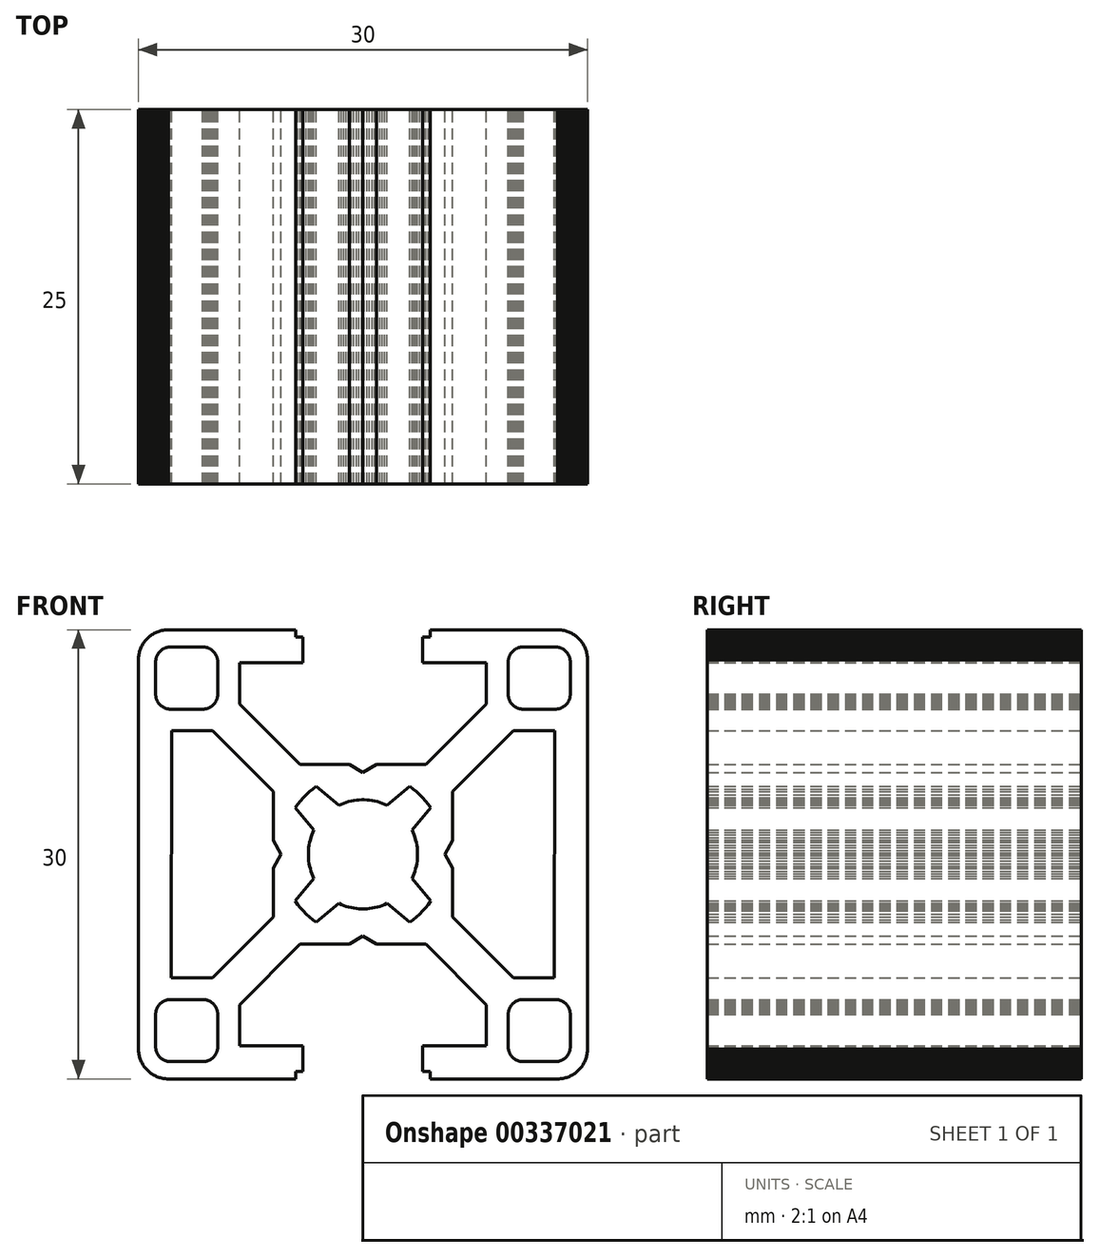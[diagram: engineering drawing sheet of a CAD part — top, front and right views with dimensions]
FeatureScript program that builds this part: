
annotation { "Feature Type Name" : "Feature", "Feature Type Description" : "" }
export const myFeature = defineFeature(function(context is Context, id is Id, definition is map)
    precondition{}
    {
        {
            var Q0;
            Q0=qCreatedBy(makeId("Front.planeOp"),FACE);
            var sketch = newSketch(context, id + "F0", { "sketchPlane" : qUnion([Q0])});
            skLineSegment(sketch, "E0", {"start": v(9.7, -12.9) * mm, "end": v(9.7, -12.85) * mm});
            skLineSegment(sketch, "E1", {"start": v(-13.85, -12.9) * mm, "end": v(-13.85, -12.85) * mm});
            skLineSegment(sketch, "E2", {"start": v(13.85, -10.7) * mm, "end": v(13.85, -10.66) * mm});
            skLineSegment(sketch, "E3", {"start": v(-9.7, -10.7) * mm, "end": v(-9.7, -10.66) * mm});
            skLineSegment(sketch, "E4", {"start": v(9.7, 10.66) * mm, "end": v(9.7, 10.7) * mm});
            skLineSegment(sketch, "E5", {"start": v(-13.85, 10.66) * mm, "end": v(-13.85, 10.7) * mm});
            skLineSegment(sketch, "E6", {"start": v(13.85, 12.85) * mm, "end": v(13.85, 12.9) * mm});
            skLineSegment(sketch, "E7", {"start": v(-9.7, 12.85) * mm, "end": v(-9.7, 12.9) * mm});
            skLineSegment(sketch, "E8", {"start": v(-15, -13.09) * mm, "end": v(-15, -13) * mm});
            skLineSegment(sketch, "E9", {"start": v(15, 13) * mm, "end": v(15, 13.09) * mm});
            skLineSegment(sketch, "E10", {"start": v(-3.64, -0.26) * mm, "end": v(-3.65, -0.09) * mm});
            skLineSegment(sketch, "E11", {"start": v(3.65, 0.09) * mm, "end": v(3.64, 0.26) * mm});
            skLineSegment(sketch, "E12", {"start": v(9.7, -12.94) * mm, "end": v(9.7, -12.9) * mm});
            skLineSegment(sketch, "E13", {"start": v(-9.7, -10.66) * mm, "end": v(-9.7, -10.61) * mm});
            skLineSegment(sketch, "E14", {"start": v(9.7, 10.61) * mm, "end": v(9.7, 10.66) * mm});
            skLineSegment(sketch, "E15", {"start": v(-9.7, 12.9) * mm, "end": v(-9.7, 12.94) * mm});
            skLineSegment(sketch, "E16", {"start": v(-15, -13.18) * mm, "end": v(-15, -13.09) * mm});
            skLineSegment(sketch, "E17", {"start": v(15, 13.09) * mm, "end": v(15, 13.18) * mm});
            skLineSegment(sketch, "E18", {"start": v(-13.85, -12.94) * mm, "end": v(-13.85, -12.9) * mm});
            skLineSegment(sketch, "E19", {"start": v(13.85, -10.66) * mm, "end": v(13.85, -10.61) * mm});
            skLineSegment(sketch, "E20", {"start": v(-13.85, 10.61) * mm, "end": v(-13.85, 10.66) * mm});
            skLineSegment(sketch, "E21", {"start": v(13.85, 12.9) * mm, "end": v(13.85, 12.94) * mm});
            skLineSegment(sketch, "E22", {"start": v(-3.62, -0.44) * mm, "end": v(-3.64, -0.26) * mm});
            skLineSegment(sketch, "E23", {"start": v(3.64, 0.26) * mm, "end": v(3.62, 0.44) * mm});
            skLineSegment(sketch, "E24", {"start": v(13.85, -10.61) * mm, "end": v(13.84, -10.57) * mm});
            skLineSegment(sketch, "E25", {"start": v(-13.84, 10.57) * mm, "end": v(-13.85, 10.61) * mm});
            skLineSegment(sketch, "E26", {"start": v(-13.84, -12.98) * mm, "end": v(-13.85, -12.94) * mm});
            skLineSegment(sketch, "E27", {"start": v(13.85, 12.94) * mm, "end": v(13.84, 12.98) * mm});
            skLineSegment(sketch, "E28", {"start": v(-14.98, -13.27) * mm, "end": v(-15, -13.18) * mm});
            skLineSegment(sketch, "E29", {"start": v(15, 13.18) * mm, "end": v(14.98, 13.27) * mm});
            skLineSegment(sketch, "E30", {"start": v(-9.7, -10.61) * mm, "end": v(-9.7, -10.57) * mm});
            skLineSegment(sketch, "E31", {"start": v(9.7, 10.57) * mm, "end": v(9.7, 10.61) * mm});
            skLineSegment(sketch, "E32", {"start": v(9.7, -12.98) * mm, "end": v(9.7, -12.94) * mm});
            skLineSegment(sketch, "E33", {"start": v(-9.7, 12.94) * mm, "end": v(-9.7, 12.98) * mm});
            skLineSegment(sketch, "E34", {"start": v(-3.6, -0.61) * mm, "end": v(-3.62, -0.44) * mm});
            skLineSegment(sketch, "E35", {"start": v(3.62, 0.44) * mm, "end": v(3.6, 0.61) * mm});
            skLineSegment(sketch, "E36", {"start": v(9.72, -13.03) * mm, "end": v(9.7, -12.98) * mm});
            skLineSegment(sketch, "E37", {"start": v(-13.83, -13.03) * mm, "end": v(-13.84, -12.98) * mm});
            skLineSegment(sketch, "E38", {"start": v(13.84, 12.98) * mm, "end": v(13.83, 13.03) * mm});
            skLineSegment(sketch, "E39", {"start": v(-9.7, 12.98) * mm, "end": v(-9.72, 13.03) * mm});
            skLineSegment(sketch, "E40", {"start": v(-14.97, -13.36) * mm, "end": v(-14.98, -13.27) * mm});
            skLineSegment(sketch, "E41", {"start": v(14.98, 13.27) * mm, "end": v(14.97, 13.36) * mm});
            skLineSegment(sketch, "E42", {"start": v(13.84, -10.57) * mm, "end": v(13.83, -10.52) * mm});
            skLineSegment(sketch, "E43", {"start": v(-9.7, -10.57) * mm, "end": v(-9.72, -10.52) * mm});
            skLineSegment(sketch, "E44", {"start": v(9.72, 10.52) * mm, "end": v(9.7, 10.57) * mm});
            skLineSegment(sketch, "E45", {"start": v(-13.83, 10.52) * mm, "end": v(-13.84, 10.57) * mm});
            skLineSegment(sketch, "E46", {"start": v(-3.56, -0.79) * mm, "end": v(-3.6, -0.61) * mm});
            skLineSegment(sketch, "E47", {"start": v(3.6, 0.61) * mm, "end": v(3.56, 0.79) * mm});
            skLineSegment(sketch, "E48", {"start": v(-14.95, -13.45) * mm, "end": v(-14.97, -13.36) * mm});
            skLineSegment(sketch, "E49", {"start": v(14.97, 13.36) * mm, "end": v(14.95, 13.45) * mm});
            skLineSegment(sketch, "E50", {"start": v(9.73, -13.07) * mm, "end": v(9.72, -13.03) * mm});
            skLineSegment(sketch, "E51", {"start": v(-13.82, -13.07) * mm, "end": v(-13.83, -13.03) * mm});
            skLineSegment(sketch, "E52", {"start": v(13.83, -10.52) * mm, "end": v(13.82, -10.48) * mm});
            skLineSegment(sketch, "E53", {"start": v(-9.72, -10.52) * mm, "end": v(-9.73, -10.48) * mm});
            skLineSegment(sketch, "E54", {"start": v(9.73, 10.48) * mm, "end": v(9.72, 10.52) * mm});
            skLineSegment(sketch, "E55", {"start": v(-13.82, 10.48) * mm, "end": v(-13.83, 10.52) * mm});
            skLineSegment(sketch, "E56", {"start": v(13.83, 13.03) * mm, "end": v(13.82, 13.07) * mm});
            skLineSegment(sketch, "E57", {"start": v(-9.72, 13.03) * mm, "end": v(-9.73, 13.07) * mm});
            skLineSegment(sketch, "E58", {"start": v(-3.52, -0.96) * mm, "end": v(-3.56, -0.79) * mm});
            skLineSegment(sketch, "E59", {"start": v(3.56, 0.79) * mm, "end": v(3.52, 0.96) * mm});
            skLineSegment(sketch, "E60", {"start": v(-14.93, -13.53) * mm, "end": v(-14.95, -13.45) * mm});
            skLineSegment(sketch, "E61", {"start": v(13.82, -10.48) * mm, "end": v(13.81, -10.43) * mm});
            skLineSegment(sketch, "E62", {"start": v(-9.73, -10.48) * mm, "end": v(-9.74, -10.43) * mm});
            skLineSegment(sketch, "E63", {"start": v(9.74, 10.43) * mm, "end": v(9.73, 10.48) * mm});
            skLineSegment(sketch, "E64", {"start": v(-13.81, 10.43) * mm, "end": v(-13.82, 10.48) * mm});
            skLineSegment(sketch, "E65", {"start": v(14.95, 13.45) * mm, "end": v(14.93, 13.53) * mm});
            skLineSegment(sketch, "E66", {"start": v(9.74, -13.12) * mm, "end": v(9.73, -13.07) * mm});
            skLineSegment(sketch, "E67", {"start": v(-13.81, -13.12) * mm, "end": v(-13.82, -13.07) * mm});
            skLineSegment(sketch, "E68", {"start": v(13.82, 13.07) * mm, "end": v(13.81, 13.12) * mm});
            skLineSegment(sketch, "E69", {"start": v(-9.73, 13.07) * mm, "end": v(-9.74, 13.12) * mm});
            skLineSegment(sketch, "E70", {"start": v(-3.47, -1.13) * mm, "end": v(-3.52, -0.96) * mm});
            skLineSegment(sketch, "E71", {"start": v(3.52, 0.96) * mm, "end": v(3.47, 1.13) * mm});
            skLineSegment(sketch, "E72", {"start": v(9.75, -13.16) * mm, "end": v(9.74, -13.12) * mm});
            skLineSegment(sketch, "E73", {"start": v(-13.8, -13.16) * mm, "end": v(-13.81, -13.12) * mm});
            skLineSegment(sketch, "E74", {"start": v(13.81, 13.12) * mm, "end": v(13.8, 13.16) * mm});
            skLineSegment(sketch, "E75", {"start": v(-9.74, 13.12) * mm, "end": v(-9.75, 13.16) * mm});
            skLineSegment(sketch, "E76", {"start": v(13.81, -10.43) * mm, "end": v(13.8, -10.4) * mm});
            skLineSegment(sketch, "E77", {"start": v(-9.74, -10.43) * mm, "end": v(-9.75, -10.4) * mm});
            skLineSegment(sketch, "E78", {"start": v(9.75, 10.4) * mm, "end": v(9.74, 10.43) * mm});
            skLineSegment(sketch, "E79", {"start": v(-13.8, 10.4) * mm, "end": v(-13.81, 10.43) * mm});
            skLineSegment(sketch, "E80", {"start": v(-14.9, -13.62) * mm, "end": v(-14.93, -13.53) * mm});
            skLineSegment(sketch, "E81", {"start": v(14.93, 13.53) * mm, "end": v(14.9, 13.62) * mm});
            skLineSegment(sketch, "E82", {"start": v(-14.87, -13.7) * mm, "end": v(-14.9, -13.62) * mm});
            skLineSegment(sketch, "E83", {"start": v(14.9, 13.62) * mm, "end": v(14.87, 13.7) * mm});
            skLineSegment(sketch, "E84", {"start": v(9.76, -13.2) * mm, "end": v(9.75, -13.16) * mm});
            skLineSegment(sketch, "E85", {"start": v(-13.79, -13.2) * mm, "end": v(-13.8, -13.16) * mm});
            skLineSegment(sketch, "E86", {"start": v(13.8, -10.4) * mm, "end": v(13.79, -10.35) * mm});
            skLineSegment(sketch, "E87", {"start": v(-9.75, -10.4) * mm, "end": v(-9.76, -10.35) * mm});
            skLineSegment(sketch, "E88", {"start": v(9.76, 10.35) * mm, "end": v(9.75, 10.4) * mm});
            skLineSegment(sketch, "E89", {"start": v(-13.79, 10.35) * mm, "end": v(-13.8, 10.4) * mm});
            skLineSegment(sketch, "E90", {"start": v(13.8, 13.16) * mm, "end": v(13.79, 13.2) * mm});
            skLineSegment(sketch, "E91", {"start": v(-9.75, 13.16) * mm, "end": v(-9.76, 13.2) * mm});
            skLineSegment(sketch, "E92", {"start": v(-3.41, -1.3) * mm, "end": v(-3.47, -1.13) * mm});
            skLineSegment(sketch, "E93", {"start": v(3.47, 1.13) * mm, "end": v(3.41, 1.3) * mm});
            skLineSegment(sketch, "E94", {"start": v(-14.84, -13.79) * mm, "end": v(-14.87, -13.7) * mm});
            skLineSegment(sketch, "E95", {"start": v(14.87, 13.7) * mm, "end": v(14.84, 13.79) * mm});
            skLineSegment(sketch, "E96", {"start": v(9.78, -13.24) * mm, "end": v(9.76, -13.2) * mm});
            skLineSegment(sketch, "E97", {"start": v(-9.76, -10.35) * mm, "end": v(-9.78, -10.3) * mm});
            skLineSegment(sketch, "E98", {"start": v(9.78, 10.3) * mm, "end": v(9.76, 10.35) * mm});
            skLineSegment(sketch, "E99", {"start": v(-9.76, 13.2) * mm, "end": v(-9.78, 13.24) * mm});
            skLineSegment(sketch, "E100", {"start": v(-13.77, -13.24) * mm, "end": v(-13.79, -13.2) * mm});
            skLineSegment(sketch, "E101", {"start": v(13.79, -10.35) * mm, "end": v(13.77, -10.3) * mm});
            skLineSegment(sketch, "E102", {"start": v(-13.77, 10.3) * mm, "end": v(-13.79, 10.35) * mm});
            skLineSegment(sketch, "E103", {"start": v(13.79, 13.2) * mm, "end": v(13.77, 13.24) * mm});
            skLineSegment(sketch, "E104", {"start": v(-3.35, -1.46) * mm, "end": v(-3.41, -1.3) * mm});
            skLineSegment(sketch, "E105", {"start": v(3.41, 1.3) * mm, "end": v(3.35, 1.46) * mm});
            skLineSegment(sketch, "E106", {"start": v(-13.75, -13.28) * mm, "end": v(-13.77, -13.24) * mm});
            skLineSegment(sketch, "E107", {"start": v(13.77, -10.3) * mm, "end": v(13.75, -10.27) * mm});
            skLineSegment(sketch, "E108", {"start": v(-13.75, 10.27) * mm, "end": v(-13.77, 10.3) * mm});
            skLineSegment(sketch, "E109", {"start": v(13.77, 13.24) * mm, "end": v(13.75, 13.28) * mm});
            skLineSegment(sketch, "E110", {"start": v(9.8, -13.28) * mm, "end": v(9.78, -13.24) * mm});
            skLineSegment(sketch, "E111", {"start": v(-9.78, -10.3) * mm, "end": v(-9.8, -10.27) * mm});
            skLineSegment(sketch, "E112", {"start": v(9.8, 10.27) * mm, "end": v(9.78, 10.3) * mm});
            skLineSegment(sketch, "E113", {"start": v(-9.78, 13.24) * mm, "end": v(-9.8, 13.28) * mm});
            skLineSegment(sketch, "E114", {"start": v(-14.8, -13.87) * mm, "end": v(-14.84, -13.79) * mm});
            skLineSegment(sketch, "E115", {"start": v(14.84, 13.79) * mm, "end": v(14.8, 13.87) * mm});
            skLineSegment(sketch, "E116", {"start": v(-3.27, -1.62) * mm, "end": v(-3.35, -1.46) * mm});
            skLineSegment(sketch, "E117", {"start": v(3.35, 1.46) * mm, "end": v(3.27, 1.62) * mm});
            skLineSegment(sketch, "E118", {"start": v(-13.73, -13.32) * mm, "end": v(-13.75, -13.28) * mm});
            skLineSegment(sketch, "E119", {"start": v(13.75, -10.27) * mm, "end": v(13.73, -10.23) * mm});
            skLineSegment(sketch, "E120", {"start": v(-13.73, 10.23) * mm, "end": v(-13.75, 10.27) * mm});
            skLineSegment(sketch, "E121", {"start": v(13.75, 13.28) * mm, "end": v(13.73, 13.32) * mm});
            skLineSegment(sketch, "E122", {"start": v(-14.76, -13.95) * mm, "end": v(-14.8, -13.87) * mm});
            skLineSegment(sketch, "E123", {"start": v(14.8, 13.87) * mm, "end": v(14.76, 13.95) * mm});
            skLineSegment(sketch, "E124", {"start": v(9.82, -13.32) * mm, "end": v(9.8, -13.28) * mm});
            skLineSegment(sketch, "E125", {"start": v(-9.8, -10.27) * mm, "end": v(-9.82, -10.23) * mm});
            skLineSegment(sketch, "E126", {"start": v(9.82, 10.23) * mm, "end": v(9.8, 10.27) * mm});
            skLineSegment(sketch, "E127", {"start": v(-9.8, 13.28) * mm, "end": v(-9.82, 13.32) * mm});
            skLineSegment(sketch, "E128", {"start": v(-9.82, -10.23) * mm, "end": v(-9.84, -10.19) * mm});
            skLineSegment(sketch, "E129", {"start": v(9.84, 10.19) * mm, "end": v(9.82, 10.23) * mm});
            skLineSegment(sketch, "E130", {"start": v(9.84, -13.36) * mm, "end": v(9.82, -13.32) * mm});
            skLineSegment(sketch, "E131", {"start": v(-9.82, 13.32) * mm, "end": v(-9.84, 13.36) * mm});
            skLineSegment(sketch, "E132", {"start": v(-14.72, -14.03) * mm, "end": v(-14.76, -13.95) * mm});
            skLineSegment(sketch, "E133", {"start": v(14.76, 13.95) * mm, "end": v(14.72, 14.03) * mm});
            skLineSegment(sketch, "E134", {"start": v(13.73, -10.23) * mm, "end": v(13.7, -10.19) * mm});
            skLineSegment(sketch, "E135", {"start": v(-13.7, 10.19) * mm, "end": v(-13.73, 10.23) * mm});
            skLineSegment(sketch, "E136", {"start": v(-13.7, -13.36) * mm, "end": v(-13.73, -13.32) * mm});
            skLineSegment(sketch, "E137", {"start": v(13.73, 13.32) * mm, "end": v(13.7, 13.36) * mm});
            skLineSegment(sketch, "E138", {"start": v(6, -0.92) * mm, "end": v(5.47, 0) * mm});
            skLineSegment(sketch, "E139", {"start": v(-5.47, 0) * mm, "end": v(-6, 0.92) * mm});
            skLineSegment(sketch, "E140", {"start": v(-13.68, -13.4) * mm, "end": v(-13.7, -13.36) * mm});
            skLineSegment(sketch, "E141", {"start": v(13.7, 13.36) * mm, "end": v(13.68, 13.4) * mm});
            skLineSegment(sketch, "E142", {"start": v(13.7, -10.19) * mm, "end": v(13.68, -10.15) * mm});
            skLineSegment(sketch, "E143", {"start": v(-13.68, 10.15) * mm, "end": v(-13.7, 10.19) * mm});
            skLineSegment(sketch, "E144", {"start": v(-14.67, -14.1) * mm, "end": v(-14.72, -14.03) * mm});
            skLineSegment(sketch, "E145", {"start": v(14.72, 14.03) * mm, "end": v(14.67, 14.1) * mm});
            skLineSegment(sketch, "E146", {"start": v(9.87, -13.4) * mm, "end": v(9.84, -13.36) * mm});
            skLineSegment(sketch, "E147", {"start": v(-9.84, 13.36) * mm, "end": v(-9.87, 13.4) * mm});
            skLineSegment(sketch, "E148", {"start": v(-9.84, -10.19) * mm, "end": v(-9.87, -10.15) * mm});
            skLineSegment(sketch, "E149", {"start": v(9.87, 10.15) * mm, "end": v(9.84, 10.19) * mm});
            skLineSegment(sketch, "E150", {"start": v(9.9, -13.44) * mm, "end": v(9.87, -13.4) * mm});
            skLineSegment(sketch, "E151", {"start": v(-13.66, -13.44) * mm, "end": v(-13.68, -13.4) * mm});
            skLineSegment(sketch, "E152", {"start": v(13.68, -10.15) * mm, "end": v(13.66, -10.11) * mm});
            skLineSegment(sketch, "E153", {"start": v(-9.87, -10.15) * mm, "end": v(-9.9, -10.11) * mm});
            skLineSegment(sketch, "E154", {"start": v(9.9, 10.11) * mm, "end": v(9.87, 10.15) * mm});
            skLineSegment(sketch, "E155", {"start": v(-13.66, 10.11) * mm, "end": v(-13.68, 10.15) * mm});
            skLineSegment(sketch, "E156", {"start": v(13.68, 13.4) * mm, "end": v(13.66, 13.44) * mm});
            skLineSegment(sketch, "E157", {"start": v(-9.87, 13.4) * mm, "end": v(-9.9, 13.44) * mm});
            skLineSegment(sketch, "E158", {"start": v(-14.62, -14.18) * mm, "end": v(-14.67, -14.1) * mm});
            skLineSegment(sketch, "E159", {"start": v(14.67, 14.1) * mm, "end": v(14.62, 14.18) * mm});
            skLineSegment(sketch, "E160", {"start": v(-4.36, -3.35) * mm, "end": v(-4.53, -3.12) * mm});
            skLineSegment(sketch, "E161", {"start": v(4.53, 3.12) * mm, "end": v(4.36, 3.35) * mm});
            skLineSegment(sketch, "E162", {"start": v(9.92, -13.47) * mm, "end": v(9.9, -13.44) * mm});
            skLineSegment(sketch, "E163", {"start": v(-9.9, -10.11) * mm, "end": v(-9.92, -10.08) * mm});
            skLineSegment(sketch, "E164", {"start": v(9.92, 10.08) * mm, "end": v(9.9, 10.11) * mm});
            skLineSegment(sketch, "E165", {"start": v(-9.9, 13.44) * mm, "end": v(-9.92, 13.47) * mm});
            skLineSegment(sketch, "E166", {"start": v(-14.56, -14.25) * mm, "end": v(-14.62, -14.18) * mm});
            skLineSegment(sketch, "E167", {"start": v(14.62, 14.18) * mm, "end": v(14.56, 14.25) * mm});
            skLineSegment(sketch, "E168", {"start": v(-13.63, -13.47) * mm, "end": v(-13.66, -13.44) * mm});
            skLineSegment(sketch, "E169", {"start": v(13.66, -10.11) * mm, "end": v(13.63, -10.08) * mm});
            skLineSegment(sketch, "E170", {"start": v(-13.63, 10.08) * mm, "end": v(-13.66, 10.11) * mm});
            skLineSegment(sketch, "E171", {"start": v(13.66, 13.44) * mm, "end": v(13.63, 13.47) * mm});
            skLineSegment(sketch, "E172", {"start": v(-4.18, -3.57) * mm, "end": v(-4.36, -3.35) * mm});
            skLineSegment(sketch, "E173", {"start": v(4.36, 3.35) * mm, "end": v(4.18, 3.57) * mm});
            skLineSegment(sketch, "E174", {"start": v(-14.5, -14.32) * mm, "end": v(-14.56, -14.25) * mm});
            skLineSegment(sketch, "E175", {"start": v(13.63, -10.08) * mm, "end": v(13.6, -10.04) * mm});
            skLineSegment(sketch, "E176", {"start": v(-13.6, 10.04) * mm, "end": v(-13.63, 10.08) * mm});
            skLineSegment(sketch, "E177", {"start": v(14.56, 14.25) * mm, "end": v(14.5, 14.32) * mm});
            skLineSegment(sketch, "E178", {"start": v(-13.6, -13.5) * mm, "end": v(-13.63, -13.47) * mm});
            skLineSegment(sketch, "E179", {"start": v(13.63, 13.47) * mm, "end": v(13.6, 13.5) * mm});
            skLineSegment(sketch, "E180", {"start": v(-9.92, -10.08) * mm, "end": v(-9.95, -10.04) * mm});
            skLineSegment(sketch, "E181", {"start": v(9.95, 10.04) * mm, "end": v(9.92, 10.08) * mm});
            skLineSegment(sketch, "E182", {"start": v(9.95, -13.5) * mm, "end": v(9.92, -13.47) * mm});
            skLineSegment(sketch, "E183", {"start": v(-9.92, 13.47) * mm, "end": v(-9.95, 13.5) * mm});
            skLineSegment(sketch, "E184", {"start": v(4.53, -3.12) * mm, "end": v(3.27, -1.62) * mm});
            skLineSegment(sketch, "E185", {"start": v(-3.27, 1.62) * mm, "end": v(-4.53, 3.12) * mm});
            skLineSegment(sketch, "E186", {"start": v(-3.99, -3.79) * mm, "end": v(-4.18, -3.57) * mm});
            skLineSegment(sketch, "E187", {"start": v(4.18, 3.57) * mm, "end": v(3.99, 3.79) * mm});
            skLineSegment(sketch, "E188", {"start": v(9.98, -13.54) * mm, "end": v(9.95, -13.5) * mm});
            skLineSegment(sketch, "E189", {"start": v(-13.57, -13.54) * mm, "end": v(-13.6, -13.5) * mm});
            skLineSegment(sketch, "E190", {"start": v(13.6, -10.04) * mm, "end": v(13.57, -10) * mm});
            skLineSegment(sketch, "E191", {"start": v(-9.95, -10.04) * mm, "end": v(-9.98, -10) * mm});
            skLineSegment(sketch, "E192", {"start": v(9.98, 10) * mm, "end": v(9.95, 10.04) * mm});
            skLineSegment(sketch, "E193", {"start": v(-13.57, 10) * mm, "end": v(-13.6, 10.04) * mm});
            skLineSegment(sketch, "E194", {"start": v(13.6, 13.5) * mm, "end": v(13.57, 13.54) * mm});
            skLineSegment(sketch, "E195", {"start": v(-9.95, 13.5) * mm, "end": v(-9.98, 13.54) * mm});
            skLineSegment(sketch, "E196", {"start": v(-14.45, -14.38) * mm, "end": v(-14.5, -14.32) * mm});
            skLineSegment(sketch, "E197", {"start": v(14.5, 14.32) * mm, "end": v(14.45, 14.38) * mm});
            skLineSegment(sketch, "E198", {"start": v(10, -13.57) * mm, "end": v(9.98, -13.54) * mm});
            skLineSegment(sketch, "E199", {"start": v(-9.98, 13.54) * mm, "end": v(-10, 13.57) * mm});
            skLineSegment(sketch, "E200", {"start": v(-14.38, -14.45) * mm, "end": v(-14.45, -14.38) * mm});
            skLineSegment(sketch, "E201", {"start": v(-13.54, -13.57) * mm, "end": v(-13.57, -13.54) * mm});
            skLineSegment(sketch, "E202", {"start": v(8.25, -10.05) * mm, "end": v(4.2, -6) * mm});
            skLineSegment(sketch, "E203", {"start": v(-9.98, -10) * mm, "end": v(-10, -9.98) * mm});
            skLineSegment(sketch, "E204", {"start": v(-3.79, -3.99) * mm, "end": v(-3.99, -3.79) * mm});
            skLineSegment(sketch, "E205", {"start": v(3.99, 3.79) * mm, "end": v(3.79, 3.99) * mm});
            skLineSegment(sketch, "E206", {"start": v(-6, 4.2) * mm, "end": v(-10.05, 8.25) * mm});
            skLineSegment(sketch, "E207", {"start": v(-4.2, 6) * mm, "end": v(-8.25, 10.05) * mm});
            skLineSegment(sketch, "E208", {"start": v(10.05, -8.25) * mm, "end": v(6, -4.2) * mm});
            skLineSegment(sketch, "E209", {"start": v(10, 9.98) * mm, "end": v(9.98, 10) * mm});
            skLineSegment(sketch, "E210", {"start": v(13.57, 13.54) * mm, "end": v(13.54, 13.57) * mm});
            skLineSegment(sketch, "E211", {"start": v(14.45, 14.38) * mm, "end": v(14.38, 14.45) * mm});
            skLineSegment(sketch, "E212", {"start": v(13.57, -10) * mm, "end": v(13.54, -9.98) * mm});
            skLineSegment(sketch, "E213", {"start": v(-13.54, 9.98) * mm, "end": v(-13.57, 10) * mm});
            skLineSegment(sketch, "E214", {"start": v(-14.32, -14.5) * mm, "end": v(-14.38, -14.45) * mm});
            skLineSegment(sketch, "E215", {"start": v(14.38, 14.45) * mm, "end": v(14.32, 14.5) * mm});
            skLineSegment(sketch, "E216", {"start": v(10.04, -13.6) * mm, "end": v(10, -13.57) * mm});
            skLineSegment(sketch, "E217", {"start": v(-13.5, -13.6) * mm, "end": v(-13.54, -13.57) * mm});
            skLineSegment(sketch, "E218", {"start": v(13.54, -9.98) * mm, "end": v(13.5, -9.95) * mm});
            skLineSegment(sketch, "E219", {"start": v(-10, -9.98) * mm, "end": v(-10.04, -9.95) * mm});
            skLineSegment(sketch, "E220", {"start": v(10.04, 9.95) * mm, "end": v(10, 9.98) * mm});
            skLineSegment(sketch, "E221", {"start": v(-13.5, 9.95) * mm, "end": v(-13.54, 9.98) * mm});
            skLineSegment(sketch, "E222", {"start": v(13.54, 13.57) * mm, "end": v(13.5, 13.6) * mm});
            skLineSegment(sketch, "E223", {"start": v(-10, 13.57) * mm, "end": v(-10.04, 13.6) * mm});
            skLineSegment(sketch, "E224", {"start": v(-3.57, -4.18) * mm, "end": v(-3.79, -3.99) * mm});
            skLineSegment(sketch, "E225", {"start": v(3.79, 3.99) * mm, "end": v(3.57, 4.18) * mm});
            skLineSegment(sketch, "E226", {"start": v(3.12, -4.53) * mm, "end": v(1.62, -3.27) * mm});
            skLineSegment(sketch, "E227", {"start": v(-1.62, 3.27) * mm, "end": v(-3.12, 4.53) * mm});
            skLineSegment(sketch, "E228", {"start": v(13.5, -9.95) * mm, "end": v(13.47, -9.92) * mm});
            skLineSegment(sketch, "E229", {"start": v(-13.47, 9.92) * mm, "end": v(-13.5, 9.95) * mm});
            skLineSegment(sketch, "E230", {"start": v(-10.04, -9.95) * mm, "end": v(-10.08, -9.92) * mm});
            skLineSegment(sketch, "E231", {"start": v(10.08, 9.92) * mm, "end": v(10.04, 9.95) * mm});
            skLineSegment(sketch, "E232", {"start": v(-13.47, -13.63) * mm, "end": v(-13.5, -13.6) * mm});
            skLineSegment(sketch, "E233", {"start": v(13.5, 13.6) * mm, "end": v(13.47, 13.63) * mm});
            skLineSegment(sketch, "E234", {"start": v(-14.25, -14.56) * mm, "end": v(-14.32, -14.5) * mm});
            skLineSegment(sketch, "E235", {"start": v(10.08, -13.63) * mm, "end": v(10.04, -13.6) * mm});
            skLineSegment(sketch, "E236", {"start": v(-10.04, 13.6) * mm, "end": v(-10.08, 13.63) * mm});
            skLineSegment(sketch, "E237", {"start": v(14.32, 14.5) * mm, "end": v(14.25, 14.56) * mm});
            skLineSegment(sketch, "E238", {"start": v(-3.35, -4.36) * mm, "end": v(-3.57, -4.18) * mm});
            skLineSegment(sketch, "E239", {"start": v(3.57, 4.18) * mm, "end": v(3.35, 4.36) * mm});
            skLineSegment(sketch, "E240", {"start": v(10.11, -13.66) * mm, "end": v(10.08, -13.63) * mm});
            skLineSegment(sketch, "E241", {"start": v(-13.44, -13.66) * mm, "end": v(-13.47, -13.63) * mm});
            skLineSegment(sketch, "E242", {"start": v(13.47, 13.63) * mm, "end": v(13.44, 13.66) * mm});
            skLineSegment(sketch, "E243", {"start": v(-10.08, 13.63) * mm, "end": v(-10.11, 13.66) * mm});
            skLineSegment(sketch, "E244", {"start": v(-14.18, -14.62) * mm, "end": v(-14.25, -14.56) * mm});
            skLineSegment(sketch, "E245", {"start": v(14.25, 14.56) * mm, "end": v(14.18, 14.62) * mm});
            skLineSegment(sketch, "E246", {"start": v(13.47, -9.92) * mm, "end": v(13.44, -9.9) * mm});
            skLineSegment(sketch, "E247", {"start": v(-10.08, -9.92) * mm, "end": v(-10.11, -9.9) * mm});
            skLineSegment(sketch, "E248", {"start": v(10.11, 9.9) * mm, "end": v(10.08, 9.92) * mm});
            skLineSegment(sketch, "E249", {"start": v(-13.44, 9.9) * mm, "end": v(-13.47, 9.92) * mm});
            skLineSegment(sketch, "E250", {"start": v(-3.12, -4.53) * mm, "end": v(-3.35, -4.36) * mm});
            skLineSegment(sketch, "E251", {"start": v(3.35, 4.36) * mm, "end": v(3.12, 4.53) * mm});
            skLineSegment(sketch, "E252", {"start": v(-14.1, -14.67) * mm, "end": v(-14.18, -14.62) * mm});
            skLineSegment(sketch, "E253", {"start": v(14.18, 14.62) * mm, "end": v(14.1, 14.67) * mm});
            skLineSegment(sketch, "E254", {"start": v(10.15, -13.68) * mm, "end": v(10.11, -13.66) * mm});
            skLineSegment(sketch, "E255", {"start": v(-13.4, -13.68) * mm, "end": v(-13.44, -13.66) * mm});
            skLineSegment(sketch, "E256", {"start": v(13.44, -9.9) * mm, "end": v(13.4, -9.87) * mm});
            skLineSegment(sketch, "E257", {"start": v(-10.11, -9.9) * mm, "end": v(-10.15, -9.87) * mm});
            skLineSegment(sketch, "E258", {"start": v(10.15, 9.87) * mm, "end": v(10.11, 9.9) * mm});
            skLineSegment(sketch, "E259", {"start": v(-13.4, 9.87) * mm, "end": v(-13.44, 9.9) * mm});
            skLineSegment(sketch, "E260", {"start": v(13.44, 13.66) * mm, "end": v(13.4, 13.68) * mm});
            skLineSegment(sketch, "E261", {"start": v(-10.11, 13.66) * mm, "end": v(-10.15, 13.68) * mm});
            skLineSegment(sketch, "E262", {"start": v(-10.15, -9.87) * mm, "end": v(-10.19, -9.84) * mm});
            skLineSegment(sketch, "E263", {"start": v(10.19, 9.84) * mm, "end": v(10.15, 9.87) * mm});
            skLineSegment(sketch, "E264", {"start": v(13.4, -9.87) * mm, "end": v(13.36, -9.84) * mm});
            skLineSegment(sketch, "E265", {"start": v(-13.36, 9.84) * mm, "end": v(-13.4, 9.87) * mm});
            skLineSegment(sketch, "E266", {"start": v(-14.03, -14.72) * mm, "end": v(-14.1, -14.67) * mm});
            skLineSegment(sketch, "E267", {"start": v(14.1, 14.67) * mm, "end": v(14.03, 14.72) * mm});
            skLineSegment(sketch, "E268", {"start": v(10.19, -13.7) * mm, "end": v(10.15, -13.68) * mm});
            skLineSegment(sketch, "E269", {"start": v(-10.15, 13.68) * mm, "end": v(-10.19, 13.7) * mm});
            skLineSegment(sketch, "E270", {"start": v(-13.36, -13.7) * mm, "end": v(-13.4, -13.68) * mm});
            skLineSegment(sketch, "E271", {"start": v(13.4, 13.68) * mm, "end": v(13.36, 13.7) * mm});
            skLineSegment(sketch, "E272", {"start": v(0.92, -6) * mm, "end": v(0, -5.47) * mm});
            skLineSegment(sketch, "E273", {"start": v(0, 5.47) * mm, "end": v(-0.92, 6) * mm});
            skLineSegment(sketch, "E274", {"start": v(-13.32, -13.73) * mm, "end": v(-13.36, -13.7) * mm});
            skLineSegment(sketch, "E275", {"start": v(13.36, 13.7) * mm, "end": v(13.32, 13.73) * mm});
            skLineSegment(sketch, "E276", {"start": v(10.23, -13.73) * mm, "end": v(10.19, -13.7) * mm});
            skLineSegment(sketch, "E277", {"start": v(-10.19, 13.7) * mm, "end": v(-10.23, 13.73) * mm});
            skLineSegment(sketch, "E278", {"start": v(-13.95, -14.76) * mm, "end": v(-14.03, -14.72) * mm});
            skLineSegment(sketch, "E279", {"start": v(14.03, 14.72) * mm, "end": v(13.95, 14.76) * mm});
            skLineSegment(sketch, "E280", {"start": v(13.36, -9.84) * mm, "end": v(13.32, -9.82) * mm});
            skLineSegment(sketch, "E281", {"start": v(-13.32, 9.82) * mm, "end": v(-13.36, 9.84) * mm});
            skLineSegment(sketch, "E282", {"start": v(-10.19, -9.84) * mm, "end": v(-10.23, -9.82) * mm});
            skLineSegment(sketch, "E283", {"start": v(10.23, 9.82) * mm, "end": v(10.19, 9.84) * mm});
            skLineSegment(sketch, "E284", {"start": v(13.32, -9.82) * mm, "end": v(13.28, -9.8) * mm});
            skLineSegment(sketch, "E285", {"start": v(-10.23, -9.82) * mm, "end": v(-10.27, -9.8) * mm});
            skLineSegment(sketch, "E286", {"start": v(10.27, 9.8) * mm, "end": v(10.23, 9.82) * mm});
            skLineSegment(sketch, "E287", {"start": v(-13.28, 9.8) * mm, "end": v(-13.32, 9.82) * mm});
            skLineSegment(sketch, "E288", {"start": v(-13.87, -14.8) * mm, "end": v(-13.95, -14.76) * mm});
            skLineSegment(sketch, "E289", {"start": v(13.95, 14.76) * mm, "end": v(13.87, 14.8) * mm});
            skLineSegment(sketch, "E290", {"start": v(10.27, -13.75) * mm, "end": v(10.23, -13.73) * mm});
            skLineSegment(sketch, "E291", {"start": v(-13.28, -13.75) * mm, "end": v(-13.32, -13.73) * mm});
            skLineSegment(sketch, "E292", {"start": v(13.32, 13.73) * mm, "end": v(13.28, 13.75) * mm});
            skLineSegment(sketch, "E293", {"start": v(-10.23, 13.73) * mm, "end": v(-10.27, 13.75) * mm});
            skLineSegment(sketch, "E294", {"start": v(-1.46, -3.35) * mm, "end": v(-1.62, -3.27) * mm});
            skLineSegment(sketch, "E295", {"start": v(1.62, 3.27) * mm, "end": v(1.46, 3.35) * mm});
            skLineSegment(sketch, "E296", {"start": v(-13.79, -14.84) * mm, "end": v(-13.87, -14.8) * mm});
            skLineSegment(sketch, "E297", {"start": v(13.87, 14.8) * mm, "end": v(13.79, 14.84) * mm});
            skLineSegment(sketch, "E298", {"start": v(13.28, -9.8) * mm, "end": v(13.24, -9.78) * mm});
            skLineSegment(sketch, "E299", {"start": v(-10.27, -9.8) * mm, "end": v(-10.3, -9.78) * mm});
            skLineSegment(sketch, "E300", {"start": v(10.3, 9.78) * mm, "end": v(10.27, 9.8) * mm});
            skLineSegment(sketch, "E301", {"start": v(-13.24, 9.78) * mm, "end": v(-13.28, 9.8) * mm});
            skLineSegment(sketch, "E302", {"start": v(10.3, -13.77) * mm, "end": v(10.27, -13.75) * mm});
            skLineSegment(sketch, "E303", {"start": v(-13.24, -13.77) * mm, "end": v(-13.28, -13.75) * mm});
            skLineSegment(sketch, "E304", {"start": v(13.28, 13.75) * mm, "end": v(13.24, 13.77) * mm});
            skLineSegment(sketch, "E305", {"start": v(-10.27, 13.75) * mm, "end": v(-10.3, 13.77) * mm});
            skLineSegment(sketch, "E306", {"start": v(-1.3, -3.41) * mm, "end": v(-1.46, -3.35) * mm});
            skLineSegment(sketch, "E307", {"start": v(1.46, 3.35) * mm, "end": v(1.3, 3.41) * mm});
            skLineSegment(sketch, "E308", {"start": v(10.35, -13.79) * mm, "end": v(10.3, -13.77) * mm});
            skLineSegment(sketch, "E309", {"start": v(-13.2, -13.79) * mm, "end": v(-13.24, -13.77) * mm});
            skLineSegment(sketch, "E310", {"start": v(13.24, 13.77) * mm, "end": v(13.2, 13.79) * mm});
            skLineSegment(sketch, "E311", {"start": v(-10.3, 13.77) * mm, "end": v(-10.35, 13.79) * mm});
            skLineSegment(sketch, "E312", {"start": v(13.24, -9.78) * mm, "end": v(13.2, -9.76) * mm});
            skLineSegment(sketch, "E313", {"start": v(-10.3, -9.78) * mm, "end": v(-10.35, -9.76) * mm});
            skLineSegment(sketch, "E314", {"start": v(10.35, 9.76) * mm, "end": v(10.3, 9.78) * mm});
            skLineSegment(sketch, "E315", {"start": v(-13.2, 9.76) * mm, "end": v(-13.24, 9.78) * mm});
            skLineSegment(sketch, "E316", {"start": v(-13.7, -14.87) * mm, "end": v(-13.79, -14.84) * mm});
            skLineSegment(sketch, "E317", {"start": v(13.79, 14.84) * mm, "end": v(13.7, 14.87) * mm});
            skLineSegment(sketch, "E318", {"start": v(-1.13, -3.47) * mm, "end": v(-1.3, -3.41) * mm});
            skLineSegment(sketch, "E319", {"start": v(1.3, 3.41) * mm, "end": v(1.13, 3.47) * mm});
            skLineSegment(sketch, "E320", {"start": v(10.4, -13.8) * mm, "end": v(10.35, -13.79) * mm});
            skLineSegment(sketch, "E321", {"start": v(-13.16, -13.8) * mm, "end": v(-13.2, -13.79) * mm});
            skLineSegment(sketch, "E322", {"start": v(13.2, -9.76) * mm, "end": v(13.16, -9.75) * mm});
            skLineSegment(sketch, "E323", {"start": v(-10.35, -9.76) * mm, "end": v(-10.4, -9.75) * mm});
            skLineSegment(sketch, "E324", {"start": v(10.4, 9.75) * mm, "end": v(10.35, 9.76) * mm});
            skLineSegment(sketch, "E325", {"start": v(-13.16, 9.75) * mm, "end": v(-13.2, 9.76) * mm});
            skLineSegment(sketch, "E326", {"start": v(13.2, 13.79) * mm, "end": v(13.16, 13.8) * mm});
            skLineSegment(sketch, "E327", {"start": v(-10.35, 13.79) * mm, "end": v(-10.4, 13.8) * mm});
            skLineSegment(sketch, "E328", {"start": v(-13.62, -14.9) * mm, "end": v(-13.7, -14.87) * mm});
            skLineSegment(sketch, "E329", {"start": v(13.7, 14.87) * mm, "end": v(13.62, 14.9) * mm});
            skLineSegment(sketch, "E330", {"start": v(-13.53, -14.93) * mm, "end": v(-13.62, -14.9) * mm});
            skLineSegment(sketch, "E331", {"start": v(13.62, 14.9) * mm, "end": v(13.53, 14.93) * mm});
            skLineSegment(sketch, "E332", {"start": v(10.43, -13.81) * mm, "end": v(10.4, -13.8) * mm});
            skLineSegment(sketch, "E333", {"start": v(-10.4, -9.75) * mm, "end": v(-10.43, -9.74) * mm});
            skLineSegment(sketch, "E334", {"start": v(10.43, 9.74) * mm, "end": v(10.4, 9.75) * mm});
            skLineSegment(sketch, "E335", {"start": v(-10.4, 13.8) * mm, "end": v(-10.43, 13.81) * mm});
            skLineSegment(sketch, "E336", {"start": v(-13.12, -13.81) * mm, "end": v(-13.16, -13.8) * mm});
            skLineSegment(sketch, "E337", {"start": v(13.16, -9.75) * mm, "end": v(13.12, -9.74) * mm});
            skLineSegment(sketch, "E338", {"start": v(-13.12, 9.74) * mm, "end": v(-13.16, 9.75) * mm});
            skLineSegment(sketch, "E339", {"start": v(13.16, 13.8) * mm, "end": v(13.12, 13.81) * mm});
            skLineSegment(sketch, "E340", {"start": v(-0.96, -3.52) * mm, "end": v(-1.13, -3.47) * mm});
            skLineSegment(sketch, "E341", {"start": v(1.13, 3.47) * mm, "end": v(0.96, 3.52) * mm});
            skLineSegment(sketch, "E342", {"start": v(-13.07, -13.82) * mm, "end": v(-13.12, -13.81) * mm});
            skLineSegment(sketch, "E343", {"start": v(13.12, -9.74) * mm, "end": v(13.07, -9.73) * mm});
            skLineSegment(sketch, "E344", {"start": v(-13.07, 9.73) * mm, "end": v(-13.12, 9.74) * mm});
            skLineSegment(sketch, "E345", {"start": v(13.12, 13.81) * mm, "end": v(13.07, 13.82) * mm});
            skLineSegment(sketch, "E346", {"start": v(-13.45, -14.95) * mm, "end": v(-13.53, -14.93) * mm});
            skLineSegment(sketch, "E347", {"start": v(10.48, -13.82) * mm, "end": v(10.43, -13.81) * mm});
            skLineSegment(sketch, "E348", {"start": v(-10.43, -9.74) * mm, "end": v(-10.48, -9.73) * mm});
            skLineSegment(sketch, "E349", {"start": v(10.48, 9.73) * mm, "end": v(10.43, 9.74) * mm});
            skLineSegment(sketch, "E350", {"start": v(-10.43, 13.81) * mm, "end": v(-10.48, 13.82) * mm});
            skLineSegment(sketch, "E351", {"start": v(13.53, 14.93) * mm, "end": v(13.45, 14.95) * mm});
            skLineSegment(sketch, "E352", {"start": v(-0.79, -3.56) * mm, "end": v(-0.96, -3.52) * mm});
            skLineSegment(sketch, "E353", {"start": v(0.96, 3.52) * mm, "end": v(0.79, 3.56) * mm});
            skLineSegment(sketch, "E354", {"start": v(10.52, -13.83) * mm, "end": v(10.48, -13.82) * mm});
            skLineSegment(sketch, "E355", {"start": v(-13.03, -13.83) * mm, "end": v(-13.07, -13.82) * mm});
            skLineSegment(sketch, "E356", {"start": v(13.07, -9.73) * mm, "end": v(13.03, -9.72) * mm});
            skLineSegment(sketch, "E357", {"start": v(-10.48, -9.73) * mm, "end": v(-10.52, -9.72) * mm});
            skLineSegment(sketch, "E358", {"start": v(10.52, 9.72) * mm, "end": v(10.48, 9.73) * mm});
            skLineSegment(sketch, "E359", {"start": v(-13.03, 9.72) * mm, "end": v(-13.07, 9.73) * mm});
            skLineSegment(sketch, "E360", {"start": v(13.07, 13.82) * mm, "end": v(13.03, 13.83) * mm});
            skLineSegment(sketch, "E361", {"start": v(-10.48, 13.82) * mm, "end": v(-10.52, 13.83) * mm});
            skLineSegment(sketch, "E362", {"start": v(-13.36, -14.97) * mm, "end": v(-13.45, -14.95) * mm});
            skLineSegment(sketch, "E363", {"start": v(13.45, 14.95) * mm, "end": v(13.36, 14.97) * mm});
            skLineSegment(sketch, "E364", {"start": v(-0.61, -3.6) * mm, "end": v(-0.79, -3.56) * mm});
            skLineSegment(sketch, "E365", {"start": v(0.79, 3.56) * mm, "end": v(0.61, 3.6) * mm});
            skLineSegment(sketch, "E366", {"start": v(10.57, -13.84) * mm, "end": v(10.52, -13.83) * mm});
            skLineSegment(sketch, "E367", {"start": v(-10.52, -9.72) * mm, "end": v(-10.57, -9.7) * mm});
            skLineSegment(sketch, "E368", {"start": v(10.57, 9.7) * mm, "end": v(10.52, 9.72) * mm});
            skLineSegment(sketch, "E369", {"start": v(-10.52, 13.83) * mm, "end": v(-10.57, 13.84) * mm});
            skLineSegment(sketch, "E370", {"start": v(-13.27, -14.98) * mm, "end": v(-13.36, -14.97) * mm});
            skLineSegment(sketch, "E371", {"start": v(13.36, 14.97) * mm, "end": v(13.27, 14.98) * mm});
            skLineSegment(sketch, "E372", {"start": v(-12.98, -13.84) * mm, "end": v(-13.03, -13.83) * mm});
            skLineSegment(sketch, "E373", {"start": v(13.03, -9.72) * mm, "end": v(12.98, -9.7) * mm});
            skLineSegment(sketch, "E374", {"start": v(-12.98, 9.7) * mm, "end": v(-13.03, 9.72) * mm});
            skLineSegment(sketch, "E375", {"start": v(13.03, 13.83) * mm, "end": v(12.98, 13.84) * mm});
            skLineSegment(sketch, "E376", {"start": v(-0.44, -3.62) * mm, "end": v(-0.61, -3.6) * mm});
            skLineSegment(sketch, "E377", {"start": v(0.61, 3.6) * mm, "end": v(0.44, 3.62) * mm});
            skLineSegment(sketch, "E378", {"start": v(12.98, -9.7) * mm, "end": v(12.94, -9.7) * mm});
            skLineSegment(sketch, "E379", {"start": v(-12.94, 9.7) * mm, "end": v(-12.98, 9.7) * mm});
            skLineSegment(sketch, "E380", {"start": v(-10.57, -9.7) * mm, "end": v(-10.61, -9.7) * mm});
            skLineSegment(sketch, "E381", {"start": v(10.61, 9.7) * mm, "end": v(10.57, 9.7) * mm});
            skLineSegment(sketch, "E382", {"start": v(-13.18, -15) * mm, "end": v(-13.27, -14.98) * mm});
            skLineSegment(sketch, "E383", {"start": v(13.27, 14.98) * mm, "end": v(13.18, 15) * mm});
            skLineSegment(sketch, "E384", {"start": v(-12.94, -13.85) * mm, "end": v(-12.98, -13.84) * mm});
            skLineSegment(sketch, "E385", {"start": v(12.98, 13.84) * mm, "end": v(12.94, 13.85) * mm});
            skLineSegment(sketch, "E386", {"start": v(10.61, -13.85) * mm, "end": v(10.57, -13.84) * mm});
            skLineSegment(sketch, "E387", {"start": v(-10.57, 13.84) * mm, "end": v(-10.61, 13.85) * mm});
            skLineSegment(sketch, "E388", {"start": v(-0.26, -3.64) * mm, "end": v(-0.44, -3.62) * mm});
            skLineSegment(sketch, "E389", {"start": v(0.44, 3.62) * mm, "end": v(0.26, 3.64) * mm});
            skLineSegment(sketch, "E390", {"start": v(-13.09, -15) * mm, "end": v(-13.18, -15) * mm});
            skLineSegment(sketch, "E391", {"start": v(10.66, -13.85) * mm, "end": v(10.61, -13.85) * mm});
            skLineSegment(sketch, "E392", {"start": v(-12.9, -13.85) * mm, "end": v(-12.94, -13.85) * mm});
            skLineSegment(sketch, "E393", {"start": v(12.94, 13.85) * mm, "end": v(12.9, 13.85) * mm});
            skLineSegment(sketch, "E394", {"start": v(-10.61, 13.85) * mm, "end": v(-10.66, 13.85) * mm});
            skLineSegment(sketch, "E395", {"start": v(13.18, 15) * mm, "end": v(13.09, 15) * mm});
            skLineSegment(sketch, "E396", {"start": v(12.94, -9.7) * mm, "end": v(12.9, -9.7) * mm});
            skLineSegment(sketch, "E397", {"start": v(-10.61, -9.7) * mm, "end": v(-10.66, -9.7) * mm});
            skLineSegment(sketch, "E398", {"start": v(10.66, 9.7) * mm, "end": v(10.61, 9.7) * mm});
            skLineSegment(sketch, "E399", {"start": v(-12.9, 9.7) * mm, "end": v(-12.94, 9.7) * mm});
            skLineSegment(sketch, "E400", {"start": v(-0.09, -3.65) * mm, "end": v(-0.26, -3.64) * mm});
            skLineSegment(sketch, "E401", {"start": v(0.26, 3.64) * mm, "end": v(0.09, 3.65) * mm});
            skLineSegment(sketch, "E402", {"start": v(-13, -15) * mm, "end": v(-13.09, -15) * mm});
            skLineSegment(sketch, "E403", {"start": v(10.7, -13.85) * mm, "end": v(10.66, -13.85) * mm});
            skLineSegment(sketch, "E404", {"start": v(-12.85, -13.85) * mm, "end": v(-12.9, -13.85) * mm});
            skLineSegment(sketch, "E405", {"start": v(12.9, -9.7) * mm, "end": v(12.85, -9.7) * mm});
            skLineSegment(sketch, "E406", {"start": v(-10.66, -9.7) * mm, "end": v(-10.7, -9.7) * mm});
            skLineSegment(sketch, "E407", {"start": v(10.7, 9.7) * mm, "end": v(10.66, 9.7) * mm});
            skLineSegment(sketch, "E408", {"start": v(-12.85, 9.7) * mm, "end": v(-12.9, 9.7) * mm});
            skLineSegment(sketch, "E409", {"start": v(12.9, 13.85) * mm, "end": v(12.85, 13.85) * mm});
            skLineSegment(sketch, "E410", {"start": v(-10.66, 13.85) * mm, "end": v(-10.7, 13.85) * mm});
            skLineSegment(sketch, "E411", {"start": v(13.09, 15) * mm, "end": v(13, 15) * mm});
            skLineSegment(sketch, "E412", {"start": v(8.25, -12.8) * mm, "end": v(4, -12.8) * mm});
            skLineSegment(sketch, "E413", {"start": v(-4, 12.8) * mm, "end": v(-8.25, 12.8) * mm});
            skLineSegment(sketch, "E414", {"start": v(-13, -15) * mm, "end": v(-4.5, -15) * mm});
            skLineSegment(sketch, "E415", {"start": v(4.5, -15) * mm, "end": v(13, -15) * mm});
            skLineSegment(sketch, "E416", {"start": v(-4.5, -14.5) * mm, "end": v(-4, -14.5) * mm});
            skLineSegment(sketch, "E417", {"start": v(4, -14.5) * mm, "end": v(4.5, -14.5) * mm});
            skLineSegment(sketch, "E418", {"start": v(10.7, -13.85) * mm, "end": v(12.85, -13.85) * mm});
            skLineSegment(sketch, "E419", {"start": v(-12.85, -13.85) * mm, "end": v(-10.7, -13.85) * mm});
            skLineSegment(sketch, "E420", {"start": v(10.7, -9.7) * mm, "end": v(12.85, -9.7) * mm});
            skLineSegment(sketch, "E421", {"start": v(-12.85, -9.7) * mm, "end": v(-10.7, -9.7) * mm});
            skLineSegment(sketch, "E422", {"start": v(10.05, -8.25) * mm, "end": v(12.8, -8.25) * mm});
            skLineSegment(sketch, "E423", {"start": v(-12.8, -8.25) * mm, "end": v(-10.05, -8.25) * mm});
            skLineSegment(sketch, "E424", {"start": v(-4.2, -6) * mm, "end": v(-0.92, -6) * mm});
            skLineSegment(sketch, "E425", {"start": v(0.92, -6) * mm, "end": v(4.2, -6) * mm});
            skLineSegment(sketch, "E426", {"start": v(-0.09, -3.65) * mm, "end": v(0.09, -3.65) * mm});
            skLineSegment(sketch, "E427", {"start": v(-0.09, 3.65) * mm, "end": v(0.09, 3.65) * mm});
            skLineSegment(sketch, "E428", {"start": v(0.92, 6) * mm, "end": v(4.2, 6) * mm});
            skLineSegment(sketch, "E429", {"start": v(-4.2, 6) * mm, "end": v(-0.92, 6) * mm});
            skLineSegment(sketch, "E430", {"start": v(10.05, 8.25) * mm, "end": v(12.8, 8.25) * mm});
            skLineSegment(sketch, "E431", {"start": v(-12.8, 8.25) * mm, "end": v(-10.05, 8.25) * mm});
            skLineSegment(sketch, "E432", {"start": v(10.7, 9.7) * mm, "end": v(12.85, 9.7) * mm});
            skLineSegment(sketch, "E433", {"start": v(-12.85, 9.7) * mm, "end": v(-10.7, 9.7) * mm});
            skLineSegment(sketch, "E434", {"start": v(10.7, 13.85) * mm, "end": v(12.85, 13.85) * mm});
            skLineSegment(sketch, "E435", {"start": v(-12.85, 13.85) * mm, "end": v(-10.7, 13.85) * mm});
            skLineSegment(sketch, "E436", {"start": v(-4.5, 14.5) * mm, "end": v(-4, 14.5) * mm});
            skLineSegment(sketch, "E437", {"start": v(4, 14.5) * mm, "end": v(4.5, 14.5) * mm});
            skLineSegment(sketch, "E438", {"start": v(-13, 15) * mm, "end": v(-4.5, 15) * mm});
            skLineSegment(sketch, "E439", {"start": v(4.5, 15) * mm, "end": v(13, 15) * mm});
            skLineSegment(sketch, "E440", {"start": v(-8.25, -12.8) * mm, "end": v(-4, -12.8) * mm});
            skLineSegment(sketch, "E441", {"start": v(4, 12.8) * mm, "end": v(8.25, 12.8) * mm});
            skLineSegment(sketch, "E442", {"start": v(13, -15) * mm, "end": v(13.09, -15) * mm});
            skLineSegment(sketch, "E443", {"start": v(12.85, -13.85) * mm, "end": v(12.9, -13.85) * mm});
            skLineSegment(sketch, "E444", {"start": v(-10.7, -13.85) * mm, "end": v(-10.66, -13.85) * mm});
            skLineSegment(sketch, "E445", {"start": v(10.66, -9.7) * mm, "end": v(10.7, -9.7) * mm});
            skLineSegment(sketch, "E446", {"start": v(-12.9, -9.7) * mm, "end": v(-12.85, -9.7) * mm});
            skLineSegment(sketch, "E447", {"start": v(12.85, 9.7) * mm, "end": v(12.9, 9.7) * mm});
            skLineSegment(sketch, "E448", {"start": v(-10.7, 9.7) * mm, "end": v(-10.66, 9.7) * mm});
            skLineSegment(sketch, "E449", {"start": v(10.66, 13.85) * mm, "end": v(10.7, 13.85) * mm});
            skLineSegment(sketch, "E450", {"start": v(-12.9, 13.85) * mm, "end": v(-12.85, 13.85) * mm});
            skLineSegment(sketch, "E451", {"start": v(-13.09, 15) * mm, "end": v(-13, 15) * mm});
            skLineSegment(sketch, "E452", {"start": v(0.09, -3.65) * mm, "end": v(0.26, -3.64) * mm});
            skLineSegment(sketch, "E453", {"start": v(-0.26, 3.64) * mm, "end": v(-0.09, 3.65) * mm});
            skLineSegment(sketch, "E454", {"start": v(10.61, -9.7) * mm, "end": v(10.66, -9.7) * mm});
            skLineSegment(sketch, "E455", {"start": v(-12.94, -9.7) * mm, "end": v(-12.9, -9.7) * mm});
            skLineSegment(sketch, "E456", {"start": v(12.9, 9.7) * mm, "end": v(12.94, 9.7) * mm});
            skLineSegment(sketch, "E457", {"start": v(-10.66, 9.7) * mm, "end": v(-10.61, 9.7) * mm});
            skLineSegment(sketch, "E458", {"start": v(13.09, -15) * mm, "end": v(13.18, -15) * mm});
            skLineSegment(sketch, "E459", {"start": v(12.9, -13.85) * mm, "end": v(12.94, -13.85) * mm});
            skLineSegment(sketch, "E460", {"start": v(-10.66, -13.85) * mm, "end": v(-10.61, -13.85) * mm});
            skLineSegment(sketch, "E461", {"start": v(10.61, 13.85) * mm, "end": v(10.66, 13.85) * mm});
            skLineSegment(sketch, "E462", {"start": v(-12.94, 13.85) * mm, "end": v(-12.9, 13.85) * mm});
            skLineSegment(sketch, "E463", {"start": v(-13.18, 15) * mm, "end": v(-13.09, 15) * mm});
            skLineSegment(sketch, "E464", {"start": v(0.26, -3.64) * mm, "end": v(0.44, -3.62) * mm});
            skLineSegment(sketch, "E465", {"start": v(-0.44, 3.62) * mm, "end": v(-0.26, 3.64) * mm});
            skLineSegment(sketch, "E466", {"start": v(-10.61, -13.85) * mm, "end": v(-10.57, -13.84) * mm});
            skLineSegment(sketch, "E467", {"start": v(10.57, 13.84) * mm, "end": v(10.61, 13.85) * mm});
            skLineSegment(sketch, "E468", {"start": v(12.94, -13.85) * mm, "end": v(12.98, -13.84) * mm});
            skLineSegment(sketch, "E469", {"start": v(-12.98, 13.84) * mm, "end": v(-12.94, 13.85) * mm});
            skLineSegment(sketch, "E470", {"start": v(13.18, -15) * mm, "end": v(13.27, -14.98) * mm});
            skLineSegment(sketch, "E471", {"start": v(-13.27, 14.98) * mm, "end": v(-13.18, 15) * mm});
            skLineSegment(sketch, "E472", {"start": v(10.57, -9.7) * mm, "end": v(10.61, -9.7) * mm});
            skLineSegment(sketch, "E473", {"start": v(-10.61, 9.7) * mm, "end": v(-10.57, 9.7) * mm});
            skLineSegment(sketch, "E474", {"start": v(-12.98, -9.7) * mm, "end": v(-12.94, -9.7) * mm});
            skLineSegment(sketch, "E475", {"start": v(12.94, 9.7) * mm, "end": v(12.98, 9.7) * mm});
            skLineSegment(sketch, "E476", {"start": v(0.44, -3.62) * mm, "end": v(0.61, -3.6) * mm});
            skLineSegment(sketch, "E477", {"start": v(-0.61, 3.6) * mm, "end": v(-0.44, 3.62) * mm});
            skLineSegment(sketch, "E478", {"start": v(12.98, -13.84) * mm, "end": v(13.03, -13.83) * mm});
            skLineSegment(sketch, "E479", {"start": v(-13.03, -9.72) * mm, "end": v(-12.98, -9.7) * mm});
            skLineSegment(sketch, "E480", {"start": v(12.98, 9.7) * mm, "end": v(13.03, 9.72) * mm});
            skLineSegment(sketch, "E481", {"start": v(-13.03, 13.83) * mm, "end": v(-12.98, 13.84) * mm});
            skLineSegment(sketch, "E482", {"start": v(13.27, -14.98) * mm, "end": v(13.36, -14.97) * mm});
            skLineSegment(sketch, "E483", {"start": v(-13.36, 14.97) * mm, "end": v(-13.27, 14.98) * mm});
            skLineSegment(sketch, "E484", {"start": v(-10.57, -13.84) * mm, "end": v(-10.52, -13.83) * mm});
            skLineSegment(sketch, "E485", {"start": v(10.52, -9.72) * mm, "end": v(10.57, -9.7) * mm});
            skLineSegment(sketch, "E486", {"start": v(-10.57, 9.7) * mm, "end": v(-10.52, 9.72) * mm});
            skLineSegment(sketch, "E487", {"start": v(10.52, 13.83) * mm, "end": v(10.57, 13.84) * mm});
            skLineSegment(sketch, "E488", {"start": v(0.61, -3.6) * mm, "end": v(0.79, -3.56) * mm});
            skLineSegment(sketch, "E489", {"start": v(-0.79, 3.56) * mm, "end": v(-0.61, 3.6) * mm});
            skLineSegment(sketch, "E490", {"start": v(13.36, -14.97) * mm, "end": v(13.45, -14.95) * mm});
            skLineSegment(sketch, "E491", {"start": v(-13.45, 14.95) * mm, "end": v(-13.36, 14.97) * mm});
            skLineSegment(sketch, "E492", {"start": v(13.03, -13.83) * mm, "end": v(13.07, -13.82) * mm});
            skLineSegment(sketch, "E493", {"start": v(-10.52, -13.83) * mm, "end": v(-10.48, -13.82) * mm});
            skLineSegment(sketch, "E494", {"start": v(10.48, -9.73) * mm, "end": v(10.52, -9.72) * mm});
            skLineSegment(sketch, "E495", {"start": v(-13.07, -9.73) * mm, "end": v(-13.03, -9.72) * mm});
            skLineSegment(sketch, "E496", {"start": v(13.03, 9.72) * mm, "end": v(13.07, 9.73) * mm});
            skLineSegment(sketch, "E497", {"start": v(-10.52, 9.72) * mm, "end": v(-10.48, 9.73) * mm});
            skLineSegment(sketch, "E498", {"start": v(10.48, 13.82) * mm, "end": v(10.52, 13.83) * mm});
            skLineSegment(sketch, "E499", {"start": v(-13.07, 13.82) * mm, "end": v(-13.03, 13.83) * mm});
            skLineSegment(sketch, "E500", {"start": v(0.79, -3.56) * mm, "end": v(0.96, -3.52) * mm});
            skLineSegment(sketch, "E501", {"start": v(-0.96, 3.52) * mm, "end": v(-0.79, 3.56) * mm});
            skLineSegment(sketch, "E502", {"start": v(13.45, -14.95) * mm, "end": v(13.53, -14.93) * mm});
            skLineSegment(sketch, "E503", {"start": v(-10.48, -13.82) * mm, "end": v(-10.43, -13.81) * mm});
            skLineSegment(sketch, "E504", {"start": v(10.43, -9.74) * mm, "end": v(10.48, -9.73) * mm});
            skLineSegment(sketch, "E505", {"start": v(-10.48, 9.73) * mm, "end": v(-10.43, 9.74) * mm});
            skLineSegment(sketch, "E506", {"start": v(10.43, 13.81) * mm, "end": v(10.48, 13.82) * mm});
            skLineSegment(sketch, "E507", {"start": v(-13.53, 14.93) * mm, "end": v(-13.45, 14.95) * mm});
            skLineSegment(sketch, "E508", {"start": v(13.07, -13.82) * mm, "end": v(13.12, -13.81) * mm});
            skLineSegment(sketch, "E509", {"start": v(-13.12, -9.74) * mm, "end": v(-13.07, -9.73) * mm});
            skLineSegment(sketch, "E510", {"start": v(13.07, 9.73) * mm, "end": v(13.12, 9.74) * mm});
            skLineSegment(sketch, "E511", {"start": v(-13.12, 13.81) * mm, "end": v(-13.07, 13.82) * mm});
            skLineSegment(sketch, "E512", {"start": v(0.96, -3.52) * mm, "end": v(1.13, -3.47) * mm});
            skLineSegment(sketch, "E513", {"start": v(-1.13, 3.47) * mm, "end": v(-0.96, 3.52) * mm});
            skLineSegment(sketch, "E514", {"start": v(13.12, -13.81) * mm, "end": v(13.16, -13.8) * mm});
            skLineSegment(sketch, "E515", {"start": v(-13.16, -9.75) * mm, "end": v(-13.12, -9.74) * mm});
            skLineSegment(sketch, "E516", {"start": v(13.12, 9.74) * mm, "end": v(13.16, 9.75) * mm});
            skLineSegment(sketch, "E517", {"start": v(-13.16, 13.8) * mm, "end": v(-13.12, 13.81) * mm});
            skLineSegment(sketch, "E518", {"start": v(-10.43, -13.81) * mm, "end": v(-10.4, -13.8) * mm});
            skLineSegment(sketch, "E519", {"start": v(10.4, -9.75) * mm, "end": v(10.43, -9.74) * mm});
            skLineSegment(sketch, "E520", {"start": v(-10.43, 9.74) * mm, "end": v(-10.4, 9.75) * mm});
            skLineSegment(sketch, "E521", {"start": v(10.4, 13.8) * mm, "end": v(10.43, 13.81) * mm});
            skLineSegment(sketch, "E522", {"start": v(13.53, -14.93) * mm, "end": v(13.62, -14.9) * mm});
            skLineSegment(sketch, "E523", {"start": v(-13.62, 14.9) * mm, "end": v(-13.53, 14.93) * mm});
            skLineSegment(sketch, "E524", {"start": v(13.62, -14.9) * mm, "end": v(13.7, -14.87) * mm});
            skLineSegment(sketch, "E525", {"start": v(-13.7, 14.87) * mm, "end": v(-13.62, 14.9) * mm});
            skLineSegment(sketch, "E526", {"start": v(13.16, -13.8) * mm, "end": v(13.2, -13.79) * mm});
            skLineSegment(sketch, "E527", {"start": v(-10.4, -13.8) * mm, "end": v(-10.35, -13.79) * mm});
            skLineSegment(sketch, "E528", {"start": v(10.35, -9.76) * mm, "end": v(10.4, -9.75) * mm});
            skLineSegment(sketch, "E529", {"start": v(-13.2, -9.76) * mm, "end": v(-13.16, -9.75) * mm});
            skLineSegment(sketch, "E530", {"start": v(13.16, 9.75) * mm, "end": v(13.2, 9.76) * mm});
            skLineSegment(sketch, "E531", {"start": v(-10.4, 9.75) * mm, "end": v(-10.35, 9.76) * mm});
            skLineSegment(sketch, "E532", {"start": v(10.35, 13.79) * mm, "end": v(10.4, 13.8) * mm});
            skLineSegment(sketch, "E533", {"start": v(-13.2, 13.79) * mm, "end": v(-13.16, 13.8) * mm});
            skLineSegment(sketch, "E534", {"start": v(1.13, -3.47) * mm, "end": v(1.3, -3.41) * mm});
            skLineSegment(sketch, "E535", {"start": v(-1.3, 3.41) * mm, "end": v(-1.13, 3.47) * mm});
            skLineSegment(sketch, "E536", {"start": v(13.7, -14.87) * mm, "end": v(13.79, -14.84) * mm});
            skLineSegment(sketch, "E537", {"start": v(-13.79, 14.84) * mm, "end": v(-13.7, 14.87) * mm});
            skLineSegment(sketch, "E538", {"start": v(10.3, -9.78) * mm, "end": v(10.35, -9.76) * mm});
            skLineSegment(sketch, "E539", {"start": v(-13.24, -9.78) * mm, "end": v(-13.2, -9.76) * mm});
            skLineSegment(sketch, "E540", {"start": v(13.2, 9.76) * mm, "end": v(13.24, 9.78) * mm});
            skLineSegment(sketch, "E541", {"start": v(-10.35, 9.76) * mm, "end": v(-10.3, 9.78) * mm});
            skLineSegment(sketch, "E542", {"start": v(13.2, -13.79) * mm, "end": v(13.24, -13.77) * mm});
            skLineSegment(sketch, "E543", {"start": v(-10.35, -13.79) * mm, "end": v(-10.3, -13.77) * mm});
            skLineSegment(sketch, "E544", {"start": v(10.3, 13.77) * mm, "end": v(10.35, 13.79) * mm});
            skLineSegment(sketch, "E545", {"start": v(-13.24, 13.77) * mm, "end": v(-13.2, 13.79) * mm});
            skLineSegment(sketch, "E546", {"start": v(1.3, -3.41) * mm, "end": v(1.46, -3.35) * mm});
            skLineSegment(sketch, "E547", {"start": v(-1.46, 3.35) * mm, "end": v(-1.3, 3.41) * mm});
            skLineSegment(sketch, "E548", {"start": v(13.24, -13.77) * mm, "end": v(13.28, -13.75) * mm});
            skLineSegment(sketch, "E549", {"start": v(-10.3, -13.77) * mm, "end": v(-10.27, -13.75) * mm});
            skLineSegment(sketch, "E550", {"start": v(10.27, 13.75) * mm, "end": v(10.3, 13.77) * mm});
            skLineSegment(sketch, "E551", {"start": v(-13.28, 13.75) * mm, "end": v(-13.24, 13.77) * mm});
            skLineSegment(sketch, "E552", {"start": v(10.27, -9.8) * mm, "end": v(10.3, -9.78) * mm});
            skLineSegment(sketch, "E553", {"start": v(-13.28, -9.8) * mm, "end": v(-13.24, -9.78) * mm});
            skLineSegment(sketch, "E554", {"start": v(13.24, 9.78) * mm, "end": v(13.28, 9.8) * mm});
            skLineSegment(sketch, "E555", {"start": v(-10.3, 9.78) * mm, "end": v(-10.27, 9.8) * mm});
            skLineSegment(sketch, "E556", {"start": v(13.79, -14.84) * mm, "end": v(13.87, -14.8) * mm});
            skLineSegment(sketch, "E557", {"start": v(-13.87, 14.8) * mm, "end": v(-13.79, 14.84) * mm});
            skLineSegment(sketch, "E558", {"start": v(1.46, -3.35) * mm, "end": v(1.62, -3.27) * mm});
            skLineSegment(sketch, "E559", {"start": v(-1.62, 3.27) * mm, "end": v(-1.46, 3.35) * mm});
            skLineSegment(sketch, "E560", {"start": v(13.28, -13.75) * mm, "end": v(13.32, -13.73) * mm});
            skLineSegment(sketch, "E561", {"start": v(-10.27, -13.75) * mm, "end": v(-10.23, -13.73) * mm});
            skLineSegment(sketch, "E562", {"start": v(10.23, 13.73) * mm, "end": v(10.27, 13.75) * mm});
            skLineSegment(sketch, "E563", {"start": v(-13.32, 13.73) * mm, "end": v(-13.28, 13.75) * mm});
            skLineSegment(sketch, "E564", {"start": v(13.87, -14.8) * mm, "end": v(13.95, -14.76) * mm});
            skLineSegment(sketch, "E565", {"start": v(-13.95, 14.76) * mm, "end": v(-13.87, 14.8) * mm});
            skLineSegment(sketch, "E566", {"start": v(10.23, -9.82) * mm, "end": v(10.27, -9.8) * mm});
            skLineSegment(sketch, "E567", {"start": v(-13.32, -9.82) * mm, "end": v(-13.28, -9.8) * mm});
            skLineSegment(sketch, "E568", {"start": v(13.28, 9.8) * mm, "end": v(13.32, 9.82) * mm});
            skLineSegment(sketch, "E569", {"start": v(-10.27, 9.8) * mm, "end": v(-10.23, 9.82) * mm});
            skLineSegment(sketch, "E570", {"start": v(10.19, -9.84) * mm, "end": v(10.23, -9.82) * mm});
            skLineSegment(sketch, "E571", {"start": v(-10.23, 9.82) * mm, "end": v(-10.19, 9.84) * mm});
            skLineSegment(sketch, "E572", {"start": v(-13.36, -9.84) * mm, "end": v(-13.32, -9.82) * mm});
            skLineSegment(sketch, "E573", {"start": v(13.32, 9.82) * mm, "end": v(13.36, 9.84) * mm});
            skLineSegment(sketch, "E574", {"start": v(13.95, -14.76) * mm, "end": v(14.03, -14.72) * mm});
            skLineSegment(sketch, "E575", {"start": v(-14.03, 14.72) * mm, "end": v(-13.95, 14.76) * mm});
            skLineSegment(sketch, "E576", {"start": v(-10.23, -13.73) * mm, "end": v(-10.19, -13.7) * mm});
            skLineSegment(sketch, "E577", {"start": v(10.19, 13.7) * mm, "end": v(10.23, 13.73) * mm});
            skLineSegment(sketch, "E578", {"start": v(13.32, -13.73) * mm, "end": v(13.36, -13.7) * mm});
            skLineSegment(sketch, "E579", {"start": v(-13.36, 13.7) * mm, "end": v(-13.32, 13.73) * mm});
            skLineSegment(sketch, "E580", {"start": v(-0.92, -6) * mm, "end": v(0, -5.47) * mm});
            skLineSegment(sketch, "E581", {"start": v(0, 5.47) * mm, "end": v(0.92, 6) * mm});
            skLineSegment(sketch, "E582", {"start": v(13.36, -13.7) * mm, "end": v(13.4, -13.68) * mm});
            skLineSegment(sketch, "E583", {"start": v(-13.4, 13.68) * mm, "end": v(-13.36, 13.7) * mm});
            skLineSegment(sketch, "E584", {"start": v(-10.19, -13.7) * mm, "end": v(-10.15, -13.68) * mm});
            skLineSegment(sketch, "E585", {"start": v(10.15, 13.68) * mm, "end": v(10.19, 13.7) * mm});
            skLineSegment(sketch, "E586", {"start": v(14.03, -14.72) * mm, "end": v(14.1, -14.67) * mm});
            skLineSegment(sketch, "E587", {"start": v(-14.1, 14.67) * mm, "end": v(-14.03, 14.72) * mm});
            skLineSegment(sketch, "E588", {"start": v(-13.4, -9.87) * mm, "end": v(-13.36, -9.84) * mm});
            skLineSegment(sketch, "E589", {"start": v(13.36, 9.84) * mm, "end": v(13.4, 9.87) * mm});
            skLineSegment(sketch, "E590", {"start": v(10.15, -9.87) * mm, "end": v(10.19, -9.84) * mm});
            skLineSegment(sketch, "E591", {"start": v(-10.19, 9.84) * mm, "end": v(-10.15, 9.87) * mm});
            skLineSegment(sketch, "E592", {"start": v(13.4, -13.68) * mm, "end": v(13.44, -13.66) * mm});
            skLineSegment(sketch, "E593", {"start": v(-10.15, -13.68) * mm, "end": v(-10.11, -13.66) * mm});
            skLineSegment(sketch, "E594", {"start": v(10.11, -9.9) * mm, "end": v(10.15, -9.87) * mm});
            skLineSegment(sketch, "E595", {"start": v(-13.44, -9.9) * mm, "end": v(-13.4, -9.87) * mm});
            skLineSegment(sketch, "E596", {"start": v(13.4, 9.87) * mm, "end": v(13.44, 9.9) * mm});
            skLineSegment(sketch, "E597", {"start": v(-10.15, 9.87) * mm, "end": v(-10.11, 9.9) * mm});
            skLineSegment(sketch, "E598", {"start": v(10.11, 13.66) * mm, "end": v(10.15, 13.68) * mm});
            skLineSegment(sketch, "E599", {"start": v(-13.44, 13.66) * mm, "end": v(-13.4, 13.68) * mm});
            skLineSegment(sketch, "E600", {"start": v(14.1, -14.67) * mm, "end": v(14.18, -14.62) * mm});
            skLineSegment(sketch, "E601", {"start": v(-14.18, 14.62) * mm, "end": v(-14.1, 14.67) * mm});
            skLineSegment(sketch, "E602", {"start": v(3.12, -4.53) * mm, "end": v(3.35, -4.36) * mm});
            skLineSegment(sketch, "E603", {"start": v(-3.35, 4.36) * mm, "end": v(-3.12, 4.53) * mm});
            skLineSegment(sketch, "E604", {"start": v(10.08, -9.92) * mm, "end": v(10.11, -9.9) * mm});
            skLineSegment(sketch, "E605", {"start": v(-13.47, -9.92) * mm, "end": v(-13.44, -9.9) * mm});
            skLineSegment(sketch, "E606", {"start": v(13.44, 9.9) * mm, "end": v(13.47, 9.92) * mm});
            skLineSegment(sketch, "E607", {"start": v(-10.11, 9.9) * mm, "end": v(-10.08, 9.92) * mm});
            skLineSegment(sketch, "E608", {"start": v(14.18, -14.62) * mm, "end": v(14.25, -14.56) * mm});
            skLineSegment(sketch, "E609", {"start": v(-14.25, 14.56) * mm, "end": v(-14.18, 14.62) * mm});
            skLineSegment(sketch, "E610", {"start": v(13.44, -13.66) * mm, "end": v(13.47, -13.63) * mm});
            skLineSegment(sketch, "E611", {"start": v(-10.11, -13.66) * mm, "end": v(-10.08, -13.63) * mm});
            skLineSegment(sketch, "E612", {"start": v(10.08, 13.63) * mm, "end": v(10.11, 13.66) * mm});
            skLineSegment(sketch, "E613", {"start": v(-13.47, 13.63) * mm, "end": v(-13.44, 13.66) * mm});
            skLineSegment(sketch, "E614", {"start": v(3.35, -4.36) * mm, "end": v(3.57, -4.18) * mm});
            skLineSegment(sketch, "E615", {"start": v(-3.57, 4.18) * mm, "end": v(-3.35, 4.36) * mm});
            skLineSegment(sketch, "E616", {"start": v(14.25, -14.56) * mm, "end": v(14.32, -14.5) * mm});
            skLineSegment(sketch, "E617", {"start": v(-10.08, -13.63) * mm, "end": v(-10.04, -13.6) * mm});
            skLineSegment(sketch, "E618", {"start": v(10.04, 13.6) * mm, "end": v(10.08, 13.63) * mm});
            skLineSegment(sketch, "E619", {"start": v(-14.32, 14.5) * mm, "end": v(-14.25, 14.56) * mm});
            skLineSegment(sketch, "E620", {"start": v(13.47, -13.63) * mm, "end": v(13.5, -13.6) * mm});
            skLineSegment(sketch, "E621", {"start": v(-13.5, 13.6) * mm, "end": v(-13.47, 13.63) * mm});
            skLineSegment(sketch, "E622", {"start": v(10.04, -9.95) * mm, "end": v(10.08, -9.92) * mm});
            skLineSegment(sketch, "E623", {"start": v(-10.08, 9.92) * mm, "end": v(-10.04, 9.95) * mm});
            skLineSegment(sketch, "E624", {"start": v(-13.5, -9.95) * mm, "end": v(-13.47, -9.92) * mm});
            skLineSegment(sketch, "E625", {"start": v(13.47, 9.92) * mm, "end": v(13.5, 9.95) * mm});
            skLineSegment(sketch, "E626", {"start": v(-3.12, -4.53) * mm, "end": v(-1.62, -3.27) * mm});
            skLineSegment(sketch, "E627", {"start": v(1.62, 3.27) * mm, "end": v(3.12, 4.53) * mm});
            skLineSegment(sketch, "E628", {"start": v(3.57, -4.18) * mm, "end": v(3.79, -3.99) * mm});
            skLineSegment(sketch, "E629", {"start": v(-3.79, 3.99) * mm, "end": v(-3.57, 4.18) * mm});
            skLineSegment(sketch, "E630", {"start": v(13.5, -13.6) * mm, "end": v(13.54, -13.57) * mm});
            skLineSegment(sketch, "E631", {"start": v(-10.04, -13.6) * mm, "end": v(-10, -13.57) * mm});
            skLineSegment(sketch, "E632", {"start": v(10, -9.98) * mm, "end": v(10.04, -9.95) * mm});
            skLineSegment(sketch, "E633", {"start": v(-13.54, -9.98) * mm, "end": v(-13.5, -9.95) * mm});
            skLineSegment(sketch, "E634", {"start": v(13.5, 9.95) * mm, "end": v(13.54, 9.98) * mm});
            skLineSegment(sketch, "E635", {"start": v(-10.04, 9.95) * mm, "end": v(-10, 9.98) * mm});
            skLineSegment(sketch, "E636", {"start": v(10, 13.57) * mm, "end": v(10.04, 13.6) * mm});
            skLineSegment(sketch, "E637", {"start": v(-13.54, 13.57) * mm, "end": v(-13.5, 13.6) * mm});
            skLineSegment(sketch, "E638", {"start": v(14.32, -14.5) * mm, "end": v(14.38, -14.45) * mm});
            skLineSegment(sketch, "E639", {"start": v(-14.38, 14.45) * mm, "end": v(-14.32, 14.5) * mm});
            skLineSegment(sketch, "E640", {"start": v(-13.57, -10) * mm, "end": v(-13.54, -9.98) * mm});
            skLineSegment(sketch, "E641", {"start": v(13.54, 9.98) * mm, "end": v(13.57, 10) * mm});
            skLineSegment(sketch, "E642", {"start": v(14.38, -14.45) * mm, "end": v(14.45, -14.38) * mm});
            skLineSegment(sketch, "E643", {"start": v(13.54, -13.57) * mm, "end": v(13.57, -13.54) * mm});
            skLineSegment(sketch, "E644", {"start": v(-8.25, -10.05) * mm, "end": v(-4.2, -6) * mm});
            skLineSegment(sketch, "E645", {"start": v(9.98, -10) * mm, "end": v(10, -9.98) * mm});
            skLineSegment(sketch, "E646", {"start": v(3.79, -3.99) * mm, "end": v(3.99, -3.79) * mm});
            skLineSegment(sketch, "E647", {"start": v(-3.99, 3.79) * mm, "end": v(-3.79, 3.99) * mm});
            skLineSegment(sketch, "E648", {"start": v(6, 4.2) * mm, "end": v(10.05, 8.25) * mm});
            skLineSegment(sketch, "E649", {"start": v(4.2, 6) * mm, "end": v(8.25, 10.05) * mm});
            skLineSegment(sketch, "E650", {"start": v(-10.05, -8.25) * mm, "end": v(-6, -4.2) * mm});
            skLineSegment(sketch, "E651", {"start": v(-10, 9.98) * mm, "end": v(-9.98, 10) * mm});
            skLineSegment(sketch, "E652", {"start": v(-13.57, 13.54) * mm, "end": v(-13.54, 13.57) * mm});
            skLineSegment(sketch, "E653", {"start": v(-14.45, 14.38) * mm, "end": v(-14.38, 14.45) * mm});
            skLineSegment(sketch, "E654", {"start": v(-10, -13.57) * mm, "end": v(-9.98, -13.54) * mm});
            skLineSegment(sketch, "E655", {"start": v(9.98, 13.54) * mm, "end": v(10, 13.57) * mm});
            skLineSegment(sketch, "E656", {"start": v(14.45, -14.38) * mm, "end": v(14.5, -14.32) * mm});
            skLineSegment(sketch, "E657", {"start": v(-14.5, 14.32) * mm, "end": v(-14.45, 14.38) * mm});
            skLineSegment(sketch, "E658", {"start": v(13.57, -13.54) * mm, "end": v(13.6, -13.5) * mm});
            skLineSegment(sketch, "E659", {"start": v(-9.98, -13.54) * mm, "end": v(-9.95, -13.5) * mm});
            skLineSegment(sketch, "E660", {"start": v(9.95, -10.04) * mm, "end": v(9.98, -10) * mm});
            skLineSegment(sketch, "E661", {"start": v(-13.6, -10.04) * mm, "end": v(-13.57, -10) * mm});
            skLineSegment(sketch, "E662", {"start": v(13.57, 10) * mm, "end": v(13.6, 10.04) * mm});
            skLineSegment(sketch, "E663", {"start": v(-9.98, 10) * mm, "end": v(-9.95, 10.04) * mm});
            skLineSegment(sketch, "E664", {"start": v(9.95, 13.5) * mm, "end": v(9.98, 13.54) * mm});
            skLineSegment(sketch, "E665", {"start": v(-13.6, 13.5) * mm, "end": v(-13.57, 13.54) * mm});
            skLineSegment(sketch, "E666", {"start": v(3.99, -3.79) * mm, "end": v(4.18, -3.57) * mm});
            skLineSegment(sketch, "E667", {"start": v(-4.18, 3.57) * mm, "end": v(-3.99, 3.79) * mm});
            skLineSegment(sketch, "E668", {"start": v(-4.53, -3.12) * mm, "end": v(-3.27, -1.62) * mm});
            skLineSegment(sketch, "E669", {"start": v(3.27, 1.62) * mm, "end": v(4.53, 3.12) * mm});
            skLineSegment(sketch, "E670", {"start": v(-9.95, -13.5) * mm, "end": v(-9.92, -13.47) * mm});
            skLineSegment(sketch, "E671", {"start": v(9.92, 13.47) * mm, "end": v(9.95, 13.5) * mm});
            skLineSegment(sketch, "E672", {"start": v(9.92, -10.08) * mm, "end": v(9.95, -10.04) * mm});
            skLineSegment(sketch, "E673", {"start": v(-9.95, 10.04) * mm, "end": v(-9.92, 10.08) * mm});
            skLineSegment(sketch, "E674", {"start": v(13.6, -13.5) * mm, "end": v(13.63, -13.47) * mm});
            skLineSegment(sketch, "E675", {"start": v(-13.63, 13.47) * mm, "end": v(-13.6, 13.5) * mm});
            skLineSegment(sketch, "E676", {"start": v(14.5, -14.32) * mm, "end": v(14.56, -14.25) * mm});
            skLineSegment(sketch, "E677", {"start": v(-13.63, -10.08) * mm, "end": v(-13.6, -10.04) * mm});
            skLineSegment(sketch, "E678", {"start": v(13.6, 10.04) * mm, "end": v(13.63, 10.08) * mm});
            skLineSegment(sketch, "E679", {"start": v(-14.56, 14.25) * mm, "end": v(-14.5, 14.32) * mm});
            skLineSegment(sketch, "E680", {"start": v(4.18, -3.57) * mm, "end": v(4.36, -3.35) * mm});
            skLineSegment(sketch, "E681", {"start": v(-4.36, 3.35) * mm, "end": v(-4.18, 3.57) * mm});
            skLineSegment(sketch, "E682", {"start": v(13.63, -13.47) * mm, "end": v(13.66, -13.44) * mm});
            skLineSegment(sketch, "E683", {"start": v(-13.66, -10.11) * mm, "end": v(-13.63, -10.08) * mm});
            skLineSegment(sketch, "E684", {"start": v(13.63, 10.08) * mm, "end": v(13.66, 10.11) * mm});
            skLineSegment(sketch, "E685", {"start": v(-13.66, 13.44) * mm, "end": v(-13.63, 13.47) * mm});
            skLineSegment(sketch, "E686", {"start": v(14.56, -14.25) * mm, "end": v(14.62, -14.18) * mm});
            skLineSegment(sketch, "E687", {"start": v(-14.62, 14.18) * mm, "end": v(-14.56, 14.25) * mm});
            skLineSegment(sketch, "E688", {"start": v(-9.92, -13.47) * mm, "end": v(-9.9, -13.44) * mm});
            skLineSegment(sketch, "E689", {"start": v(9.9, -10.11) * mm, "end": v(9.92, -10.08) * mm});
            skLineSegment(sketch, "E690", {"start": v(-9.92, 10.08) * mm, "end": v(-9.9, 10.11) * mm});
            skLineSegment(sketch, "E691", {"start": v(9.9, 13.44) * mm, "end": v(9.92, 13.47) * mm});
            skLineSegment(sketch, "E692", {"start": v(4.36, -3.35) * mm, "end": v(4.53, -3.12) * mm});
            skLineSegment(sketch, "E693", {"start": v(-4.53, 3.12) * mm, "end": v(-4.36, 3.35) * mm});
            skLineSegment(sketch, "E694", {"start": v(14.62, -14.18) * mm, "end": v(14.67, -14.1) * mm});
            skLineSegment(sketch, "E695", {"start": v(-14.67, 14.1) * mm, "end": v(-14.62, 14.18) * mm});
            skLineSegment(sketch, "E696", {"start": v(13.66, -13.44) * mm, "end": v(13.68, -13.4) * mm});
            skLineSegment(sketch, "E697", {"start": v(-9.9, -13.44) * mm, "end": v(-9.87, -13.4) * mm});
            skLineSegment(sketch, "E698", {"start": v(9.87, -10.15) * mm, "end": v(9.9, -10.11) * mm});
            skLineSegment(sketch, "E699", {"start": v(-13.68, -10.15) * mm, "end": v(-13.66, -10.11) * mm});
            skLineSegment(sketch, "E700", {"start": v(13.66, 10.11) * mm, "end": v(13.68, 10.15) * mm});
            skLineSegment(sketch, "E701", {"start": v(-9.9, 10.11) * mm, "end": v(-9.87, 10.15) * mm});
            skLineSegment(sketch, "E702", {"start": v(9.87, 13.4) * mm, "end": v(9.9, 13.44) * mm});
            skLineSegment(sketch, "E703", {"start": v(-13.68, 13.4) * mm, "end": v(-13.66, 13.44) * mm});
            skLineSegment(sketch, "E704", {"start": v(9.84, -10.19) * mm, "end": v(9.87, -10.15) * mm});
            skLineSegment(sketch, "E705", {"start": v(-9.87, 10.15) * mm, "end": v(-9.84, 10.19) * mm});
            skLineSegment(sketch, "E706", {"start": v(-9.87, -13.4) * mm, "end": v(-9.84, -13.36) * mm});
            skLineSegment(sketch, "E707", {"start": v(9.84, 13.36) * mm, "end": v(9.87, 13.4) * mm});
            skLineSegment(sketch, "E708", {"start": v(14.67, -14.1) * mm, "end": v(14.72, -14.03) * mm});
            skLineSegment(sketch, "E709", {"start": v(-14.72, 14.03) * mm, "end": v(-14.67, 14.1) * mm});
            skLineSegment(sketch, "E710", {"start": v(-13.7, -10.19) * mm, "end": v(-13.68, -10.15) * mm});
            skLineSegment(sketch, "E711", {"start": v(13.68, 10.15) * mm, "end": v(13.7, 10.19) * mm});
            skLineSegment(sketch, "E712", {"start": v(13.68, -13.4) * mm, "end": v(13.7, -13.36) * mm});
            skLineSegment(sketch, "E713", {"start": v(-13.7, 13.36) * mm, "end": v(-13.68, 13.4) * mm});
            skLineSegment(sketch, "E714", {"start": v(-6, -0.92) * mm, "end": v(-5.47, 0) * mm});
            skLineSegment(sketch, "E715", {"start": v(5.47, 0) * mm, "end": v(6, 0.92) * mm});
            skLineSegment(sketch, "E716", {"start": v(13.7, -13.36) * mm, "end": v(13.73, -13.32) * mm});
            skLineSegment(sketch, "E717", {"start": v(-13.73, 13.32) * mm, "end": v(-13.7, 13.36) * mm});
            skLineSegment(sketch, "E718", {"start": v(-13.73, -10.23) * mm, "end": v(-13.7, -10.19) * mm});
            skLineSegment(sketch, "E719", {"start": v(13.7, 10.19) * mm, "end": v(13.73, 10.23) * mm});
            skLineSegment(sketch, "E720", {"start": v(14.72, -14.03) * mm, "end": v(14.76, -13.95) * mm});
            skLineSegment(sketch, "E721", {"start": v(-14.76, 13.95) * mm, "end": v(-14.72, 14.03) * mm});
            skLineSegment(sketch, "E722", {"start": v(-9.84, -13.36) * mm, "end": v(-9.82, -13.32) * mm});
            skLineSegment(sketch, "E723", {"start": v(9.82, 13.32) * mm, "end": v(9.84, 13.36) * mm});
            skLineSegment(sketch, "E724", {"start": v(9.82, -10.23) * mm, "end": v(9.84, -10.19) * mm});
            skLineSegment(sketch, "E725", {"start": v(-9.84, 10.19) * mm, "end": v(-9.82, 10.23) * mm});
            skLineSegment(sketch, "E726", {"start": v(-9.82, -13.32) * mm, "end": v(-9.8, -13.28) * mm});
            skLineSegment(sketch, "E727", {"start": v(9.8, -10.27) * mm, "end": v(9.82, -10.23) * mm});
            skLineSegment(sketch, "E728", {"start": v(-9.82, 10.23) * mm, "end": v(-9.8, 10.27) * mm});
            skLineSegment(sketch, "E729", {"start": v(9.8, 13.28) * mm, "end": v(9.82, 13.32) * mm});
            skLineSegment(sketch, "E730", {"start": v(14.76, -13.95) * mm, "end": v(14.8, -13.87) * mm});
            skLineSegment(sketch, "E731", {"start": v(-14.8, 13.87) * mm, "end": v(-14.76, 13.95) * mm});
            skLineSegment(sketch, "E732", {"start": v(13.73, -13.32) * mm, "end": v(13.75, -13.28) * mm});
            skLineSegment(sketch, "E733", {"start": v(-13.75, -10.27) * mm, "end": v(-13.73, -10.23) * mm});
            skLineSegment(sketch, "E734", {"start": v(13.73, 10.23) * mm, "end": v(13.75, 10.27) * mm});
            skLineSegment(sketch, "E735", {"start": v(-13.75, 13.28) * mm, "end": v(-13.73, 13.32) * mm});
            skLineSegment(sketch, "E736", {"start": v(3.27, -1.62) * mm, "end": v(3.35, -1.46) * mm});
            skLineSegment(sketch, "E737", {"start": v(-3.35, 1.46) * mm, "end": v(-3.27, 1.62) * mm});
            skLineSegment(sketch, "E738", {"start": v(14.8, -13.87) * mm, "end": v(14.84, -13.79) * mm});
            skLineSegment(sketch, "E739", {"start": v(-14.84, 13.79) * mm, "end": v(-14.8, 13.87) * mm});
            skLineSegment(sketch, "E740", {"start": v(-9.8, -13.28) * mm, "end": v(-9.78, -13.24) * mm});
            skLineSegment(sketch, "E741", {"start": v(9.78, -10.3) * mm, "end": v(9.8, -10.27) * mm});
            skLineSegment(sketch, "E742", {"start": v(-9.8, 10.27) * mm, "end": v(-9.78, 10.3) * mm});
            skLineSegment(sketch, "E743", {"start": v(9.78, 13.24) * mm, "end": v(9.8, 13.28) * mm});
            skLineSegment(sketch, "E744", {"start": v(13.75, -13.28) * mm, "end": v(13.77, -13.24) * mm});
            skLineSegment(sketch, "E745", {"start": v(-13.77, -10.3) * mm, "end": v(-13.75, -10.27) * mm});
            skLineSegment(sketch, "E746", {"start": v(13.75, 10.27) * mm, "end": v(13.77, 10.3) * mm});
            skLineSegment(sketch, "E747", {"start": v(-13.77, 13.24) * mm, "end": v(-13.75, 13.28) * mm});
            skLineSegment(sketch, "E748", {"start": v(3.35, -1.46) * mm, "end": v(3.41, -1.3) * mm});
            skLineSegment(sketch, "E749", {"start": v(-3.41, 1.3) * mm, "end": v(-3.35, 1.46) * mm});
            skLineSegment(sketch, "E750", {"start": v(13.77, -13.24) * mm, "end": v(13.79, -13.2) * mm});
            skLineSegment(sketch, "E751", {"start": v(-13.79, -10.35) * mm, "end": v(-13.77, -10.3) * mm});
            skLineSegment(sketch, "E752", {"start": v(13.77, 10.3) * mm, "end": v(13.79, 10.35) * mm});
            skLineSegment(sketch, "E753", {"start": v(-13.79, 13.2) * mm, "end": v(-13.77, 13.24) * mm});
            skLineSegment(sketch, "E754", {"start": v(-9.78, -13.24) * mm, "end": v(-9.76, -13.2) * mm});
            skLineSegment(sketch, "E755", {"start": v(9.76, -10.35) * mm, "end": v(9.78, -10.3) * mm});
            skLineSegment(sketch, "E756", {"start": v(-9.78, 10.3) * mm, "end": v(-9.76, 10.35) * mm});
            skLineSegment(sketch, "E757", {"start": v(9.76, 13.2) * mm, "end": v(9.78, 13.24) * mm});
            skLineSegment(sketch, "E758", {"start": v(14.84, -13.79) * mm, "end": v(14.87, -13.7) * mm});
            skLineSegment(sketch, "E759", {"start": v(-14.87, 13.7) * mm, "end": v(-14.84, 13.79) * mm});
            skLineSegment(sketch, "E760", {"start": v(3.41, -1.3) * mm, "end": v(3.47, -1.13) * mm});
            skLineSegment(sketch, "E761", {"start": v(-3.47, 1.13) * mm, "end": v(-3.41, 1.3) * mm});
            skLineSegment(sketch, "E762", {"start": v(13.79, -13.2) * mm, "end": v(13.8, -13.16) * mm});
            skLineSegment(sketch, "E763", {"start": v(-9.76, -13.2) * mm, "end": v(-9.75, -13.16) * mm});
            skLineSegment(sketch, "E764", {"start": v(9.75, -10.4) * mm, "end": v(9.76, -10.35) * mm});
            skLineSegment(sketch, "E765", {"start": v(-13.8, -10.4) * mm, "end": v(-13.79, -10.35) * mm});
            skLineSegment(sketch, "E766", {"start": v(13.79, 10.35) * mm, "end": v(13.8, 10.4) * mm});
            skLineSegment(sketch, "E767", {"start": v(-9.76, 10.35) * mm, "end": v(-9.75, 10.4) * mm});
            skLineSegment(sketch, "E768", {"start": v(9.75, 13.16) * mm, "end": v(9.76, 13.2) * mm});
            skLineSegment(sketch, "E769", {"start": v(-13.8, 13.16) * mm, "end": v(-13.79, 13.2) * mm});
            skLineSegment(sketch, "E770", {"start": v(14.87, -13.7) * mm, "end": v(14.9, -13.62) * mm});
            skLineSegment(sketch, "E771", {"start": v(-14.9, 13.62) * mm, "end": v(-14.87, 13.7) * mm});
            skLineSegment(sketch, "E772", {"start": v(14.9, -13.62) * mm, "end": v(14.93, -13.53) * mm});
            skLineSegment(sketch, "E773", {"start": v(-14.93, 13.53) * mm, "end": v(-14.9, 13.62) * mm});
            skLineSegment(sketch, "E774", {"start": v(9.74, -10.43) * mm, "end": v(9.75, -10.4) * mm});
            skLineSegment(sketch, "E775", {"start": v(-13.81, -10.43) * mm, "end": v(-13.8, -10.4) * mm});
            skLineSegment(sketch, "E776", {"start": v(13.8, 10.4) * mm, "end": v(13.81, 10.43) * mm});
            skLineSegment(sketch, "E777", {"start": v(-9.75, 10.4) * mm, "end": v(-9.74, 10.43) * mm});
            skLineSegment(sketch, "E778", {"start": v(13.8, -13.16) * mm, "end": v(13.81, -13.12) * mm});
            skLineSegment(sketch, "E779", {"start": v(-9.75, -13.16) * mm, "end": v(-9.74, -13.12) * mm});
            skLineSegment(sketch, "E780", {"start": v(9.74, 13.12) * mm, "end": v(9.75, 13.16) * mm});
            skLineSegment(sketch, "E781", {"start": v(-13.81, 13.12) * mm, "end": v(-13.8, 13.16) * mm});
            skLineSegment(sketch, "E782", {"start": v(3.47, -1.13) * mm, "end": v(3.52, -0.96) * mm});
            skLineSegment(sketch, "E783", {"start": v(-3.52, 0.96) * mm, "end": v(-3.47, 1.13) * mm});
            skLineSegment(sketch, "E784", {"start": v(13.81, -13.12) * mm, "end": v(13.82, -13.07) * mm});
            skLineSegment(sketch, "E785", {"start": v(-9.74, -13.12) * mm, "end": v(-9.73, -13.07) * mm});
            skLineSegment(sketch, "E786", {"start": v(9.73, 13.07) * mm, "end": v(9.74, 13.12) * mm});
            skLineSegment(sketch, "E787", {"start": v(-13.82, 13.07) * mm, "end": v(-13.81, 13.12) * mm});
            skLineSegment(sketch, "E788", {"start": v(14.93, -13.53) * mm, "end": v(14.95, -13.45) * mm});
            skLineSegment(sketch, "E789", {"start": v(9.73, -10.48) * mm, "end": v(9.74, -10.43) * mm});
            skLineSegment(sketch, "E790", {"start": v(-13.82, -10.48) * mm, "end": v(-13.81, -10.43) * mm});
            skLineSegment(sketch, "E791", {"start": v(13.81, 10.43) * mm, "end": v(13.82, 10.48) * mm});
            skLineSegment(sketch, "E792", {"start": v(-9.74, 10.43) * mm, "end": v(-9.73, 10.48) * mm});
            skLineSegment(sketch, "E793", {"start": v(-14.95, 13.45) * mm, "end": v(-14.93, 13.53) * mm});
            skLineSegment(sketch, "E794", {"start": v(3.52, -0.96) * mm, "end": v(3.56, -0.79) * mm});
            skLineSegment(sketch, "E795", {"start": v(-3.56, 0.79) * mm, "end": v(-3.52, 0.96) * mm});
            skLineSegment(sketch, "E796", {"start": v(13.82, -13.07) * mm, "end": v(13.83, -13.03) * mm});
            skLineSegment(sketch, "E797", {"start": v(-9.73, -13.07) * mm, "end": v(-9.72, -13.03) * mm});
            skLineSegment(sketch, "E798", {"start": v(9.72, -10.52) * mm, "end": v(9.73, -10.48) * mm});
            skLineSegment(sketch, "E799", {"start": v(-13.83, -10.52) * mm, "end": v(-13.82, -10.48) * mm});
            skLineSegment(sketch, "E800", {"start": v(13.82, 10.48) * mm, "end": v(13.83, 10.52) * mm});
            skLineSegment(sketch, "E801", {"start": v(-9.73, 10.48) * mm, "end": v(-9.72, 10.52) * mm});
            skLineSegment(sketch, "E802", {"start": v(9.72, 13.03) * mm, "end": v(9.73, 13.07) * mm});
            skLineSegment(sketch, "E803", {"start": v(-13.83, 13.03) * mm, "end": v(-13.82, 13.07) * mm});
            skLineSegment(sketch, "E804", {"start": v(14.95, -13.45) * mm, "end": v(14.97, -13.36) * mm});
            skLineSegment(sketch, "E805", {"start": v(-14.97, 13.36) * mm, "end": v(-14.95, 13.45) * mm});
            skLineSegment(sketch, "E806", {"start": v(3.56, -0.79) * mm, "end": v(3.6, -0.61) * mm});
            skLineSegment(sketch, "E807", {"start": v(-3.6, 0.61) * mm, "end": v(-3.56, 0.79) * mm});
            skLineSegment(sketch, "E808", {"start": v(9.7, -10.57) * mm, "end": v(9.72, -10.52) * mm});
            skLineSegment(sketch, "E809", {"start": v(-13.84, -10.57) * mm, "end": v(-13.83, -10.52) * mm});
            skLineSegment(sketch, "E810", {"start": v(13.83, 10.52) * mm, "end": v(13.84, 10.57) * mm});
            skLineSegment(sketch, "E811", {"start": v(-9.72, 10.52) * mm, "end": v(-9.7, 10.57) * mm});
            skLineSegment(sketch, "E812", {"start": v(14.97, -13.36) * mm, "end": v(14.98, -13.27) * mm});
            skLineSegment(sketch, "E813", {"start": v(-14.98, 13.27) * mm, "end": v(-14.97, 13.36) * mm});
            skLineSegment(sketch, "E814", {"start": v(13.83, -13.03) * mm, "end": v(13.84, -12.98) * mm});
            skLineSegment(sketch, "E815", {"start": v(-9.72, -13.03) * mm, "end": v(-9.7, -12.98) * mm});
            skLineSegment(sketch, "E816", {"start": v(9.7, 12.98) * mm, "end": v(9.72, 13.03) * mm});
            skLineSegment(sketch, "E817", {"start": v(-13.84, 12.98) * mm, "end": v(-13.83, 13.03) * mm});
            skLineSegment(sketch, "E818", {"start": v(3.6, -0.61) * mm, "end": v(3.62, -0.44) * mm});
            skLineSegment(sketch, "E819", {"start": v(-3.62, 0.44) * mm, "end": v(-3.6, 0.61) * mm});
            skLineSegment(sketch, "E820", {"start": v(-9.7, -12.98) * mm, "end": v(-9.7, -12.94) * mm});
            skLineSegment(sketch, "E821", {"start": v(9.7, 12.94) * mm, "end": v(9.7, 12.98) * mm});
            skLineSegment(sketch, "E822", {"start": v(9.7, -10.61) * mm, "end": v(9.7, -10.57) * mm});
            skLineSegment(sketch, "E823", {"start": v(-9.7, 10.57) * mm, "end": v(-9.7, 10.61) * mm});
            skLineSegment(sketch, "E824", {"start": v(14.98, -13.27) * mm, "end": v(15, -13.18) * mm});
            skLineSegment(sketch, "E825", {"start": v(-15, 13.18) * mm, "end": v(-14.98, 13.27) * mm});
            skLineSegment(sketch, "E826", {"start": v(13.84, -12.98) * mm, "end": v(13.85, -12.94) * mm});
            skLineSegment(sketch, "E827", {"start": v(-13.85, 12.94) * mm, "end": v(-13.84, 12.98) * mm});
            skLineSegment(sketch, "E828", {"start": v(-13.85, -10.61) * mm, "end": v(-13.84, -10.57) * mm});
            skLineSegment(sketch, "E829", {"start": v(13.84, 10.57) * mm, "end": v(13.85, 10.61) * mm});
            skLineSegment(sketch, "E830", {"start": v(3.62, -0.44) * mm, "end": v(3.64, -0.26) * mm});
            skLineSegment(sketch, "E831", {"start": v(-3.64, 0.26) * mm, "end": v(-3.62, 0.44) * mm});
            skLineSegment(sketch, "E832", {"start": v(13.85, -12.94) * mm, "end": v(13.85, -12.9) * mm});
            skLineSegment(sketch, "E833", {"start": v(-13.85, -10.66) * mm, "end": v(-13.85, -10.61) * mm});
            skLineSegment(sketch, "E834", {"start": v(13.85, 10.61) * mm, "end": v(13.85, 10.66) * mm});
            skLineSegment(sketch, "E835", {"start": v(-13.85, 12.9) * mm, "end": v(-13.85, 12.94) * mm});
            skLineSegment(sketch, "E836", {"start": v(15, -13.18) * mm, "end": v(15, -13.09) * mm});
            skLineSegment(sketch, "E837", {"start": v(-15, 13.09) * mm, "end": v(-15, 13.18) * mm});
            skLineSegment(sketch, "E838", {"start": v(-9.7, -12.94) * mm, "end": v(-9.7, -12.9) * mm});
            skLineSegment(sketch, "E839", {"start": v(9.7, -10.66) * mm, "end": v(9.7, -10.61) * mm});
            skLineSegment(sketch, "E840", {"start": v(-9.7, 10.61) * mm, "end": v(-9.7, 10.66) * mm});
            skLineSegment(sketch, "E841", {"start": v(9.7, 12.9) * mm, "end": v(9.7, 12.94) * mm});
            skLineSegment(sketch, "E842", {"start": v(3.64, -0.26) * mm, "end": v(3.65, -0.09) * mm});
            skLineSegment(sketch, "E843", {"start": v(-3.65, 0.09) * mm, "end": v(-3.64, 0.26) * mm});
            skLineSegment(sketch, "E844", {"start": v(15, -13.09) * mm, "end": v(15, -13) * mm});
            skLineSegment(sketch, "E845", {"start": v(-15, 13) * mm, "end": v(-15, 13.09) * mm});
            skLineSegment(sketch, "E846", {"start": v(13.85, -12.9) * mm, "end": v(13.85, -12.85) * mm});
            skLineSegment(sketch, "E847", {"start": v(-9.7, -12.9) * mm, "end": v(-9.7, -12.85) * mm});
            skLineSegment(sketch, "E848", {"start": v(9.7, -10.7) * mm, "end": v(9.7, -10.66) * mm});
            skLineSegment(sketch, "E849", {"start": v(-13.85, -10.7) * mm, "end": v(-13.85, -10.66) * mm});
            skLineSegment(sketch, "E850", {"start": v(13.85, 10.66) * mm, "end": v(13.85, 10.7) * mm});
            skLineSegment(sketch, "E851", {"start": v(-9.7, 10.66) * mm, "end": v(-9.7, 10.7) * mm});
            skLineSegment(sketch, "E852", {"start": v(9.7, 12.85) * mm, "end": v(9.7, 12.9) * mm});
            skLineSegment(sketch, "E853", {"start": v(-13.85, 12.85) * mm, "end": v(-13.85, 12.9) * mm});
            skLineSegment(sketch, "E854", {"start": v(12.8, -8.25) * mm, "end": v(12.8, 8.25) * mm});
            skLineSegment(sketch, "E855", {"start": v(-12.8, -8.25) * mm, "end": v(-12.8, 8.25) * mm});
            skLineSegment(sketch, "E856", {"start": v(-15, -13) * mm, "end": v(-15, 13) * mm});
            skLineSegment(sketch, "E857", {"start": v(-13.85, -12.85) * mm, "end": v(-13.85, -10.7) * mm});
            skLineSegment(sketch, "E858", {"start": v(-13.85, 10.7) * mm, "end": v(-13.85, 12.85) * mm});
            skLineSegment(sketch, "E859", {"start": v(-9.7, -12.85) * mm, "end": v(-9.7, -10.7) * mm});
            skLineSegment(sketch, "E860", {"start": v(-9.7, 10.7) * mm, "end": v(-9.7, 12.85) * mm});
            skLineSegment(sketch, "E861", {"start": v(-8.25, 10.05) * mm, "end": v(-8.25, 12.8) * mm});
            skLineSegment(sketch, "E862", {"start": v(-8.25, -12.8) * mm, "end": v(-8.25, -10.05) * mm});
            skLineSegment(sketch, "E863", {"start": v(-6, -4.2) * mm, "end": v(-6, -0.92) * mm});
            skLineSegment(sketch, "E864", {"start": v(-6, 0.92) * mm, "end": v(-6, 4.2) * mm});
            skLineSegment(sketch, "E865", {"start": v(-4.5, 14.5) * mm, "end": v(-4.5, 15) * mm});
            skLineSegment(sketch, "E866", {"start": v(-4.5, -15) * mm, "end": v(-4.5, -14.5) * mm});
            skLineSegment(sketch, "E867", {"start": v(-4, 12.8) * mm, "end": v(-4, 14.5) * mm});
            skLineSegment(sketch, "E868", {"start": v(-4, -14.5) * mm, "end": v(-4, -12.8) * mm});
            skLineSegment(sketch, "E869", {"start": v(-3.65, -0.09) * mm, "end": v(-3.65, 0.09) * mm});
            skLineSegment(sketch, "E870", {"start": v(3.65, -0.09) * mm, "end": v(3.65, 0.09) * mm});
            skLineSegment(sketch, "E871", {"start": v(4, -14.5) * mm, "end": v(4, -12.8) * mm});
            skLineSegment(sketch, "E872", {"start": v(4, 12.8) * mm, "end": v(4, 14.5) * mm});
            skLineSegment(sketch, "E873", {"start": v(4.5, -15) * mm, "end": v(4.5, -14.5) * mm});
            skLineSegment(sketch, "E874", {"start": v(4.5, 14.5) * mm, "end": v(4.5, 15) * mm});
            skLineSegment(sketch, "E875", {"start": v(6, 0.92) * mm, "end": v(6, 4.2) * mm});
            skLineSegment(sketch, "E876", {"start": v(6, -4.2) * mm, "end": v(6, -0.92) * mm});
            skLineSegment(sketch, "E877", {"start": v(8.25, -12.8) * mm, "end": v(8.25, -10.05) * mm});
            skLineSegment(sketch, "E878", {"start": v(8.25, 10.05) * mm, "end": v(8.25, 12.8) * mm});
            skLineSegment(sketch, "E879", {"start": v(9.7, 10.7) * mm, "end": v(9.7, 12.85) * mm});
            skLineSegment(sketch, "E880", {"start": v(9.7, -12.85) * mm, "end": v(9.7, -10.7) * mm});
            skLineSegment(sketch, "E881", {"start": v(13.85, 10.7) * mm, "end": v(13.85, 12.85) * mm});
            skLineSegment(sketch, "E882", {"start": v(13.85, -12.85) * mm, "end": v(13.85, -10.7) * mm});
            skLineSegment(sketch, "E883", {"start": v(15, -13) * mm, "end": v(15, 13) * mm});
            skSolve(sketch);
        }
        {
            var Q0;
            Q0=makeQuery(id+"F0.imprint","IMPRINT",FACE,{"disambiguationData":[TD([[makeQuery(id+"F0.imprint","IMPRINT",EDGE,{"derivedFrom":sQuery(id+"F0.wireOp",EDGE,"E0")}),1.0]])]});
            extrude(context, id + "F1", {"entities" : qUnion([Q0]), "depth" : 25 * mm});
        }
    });
